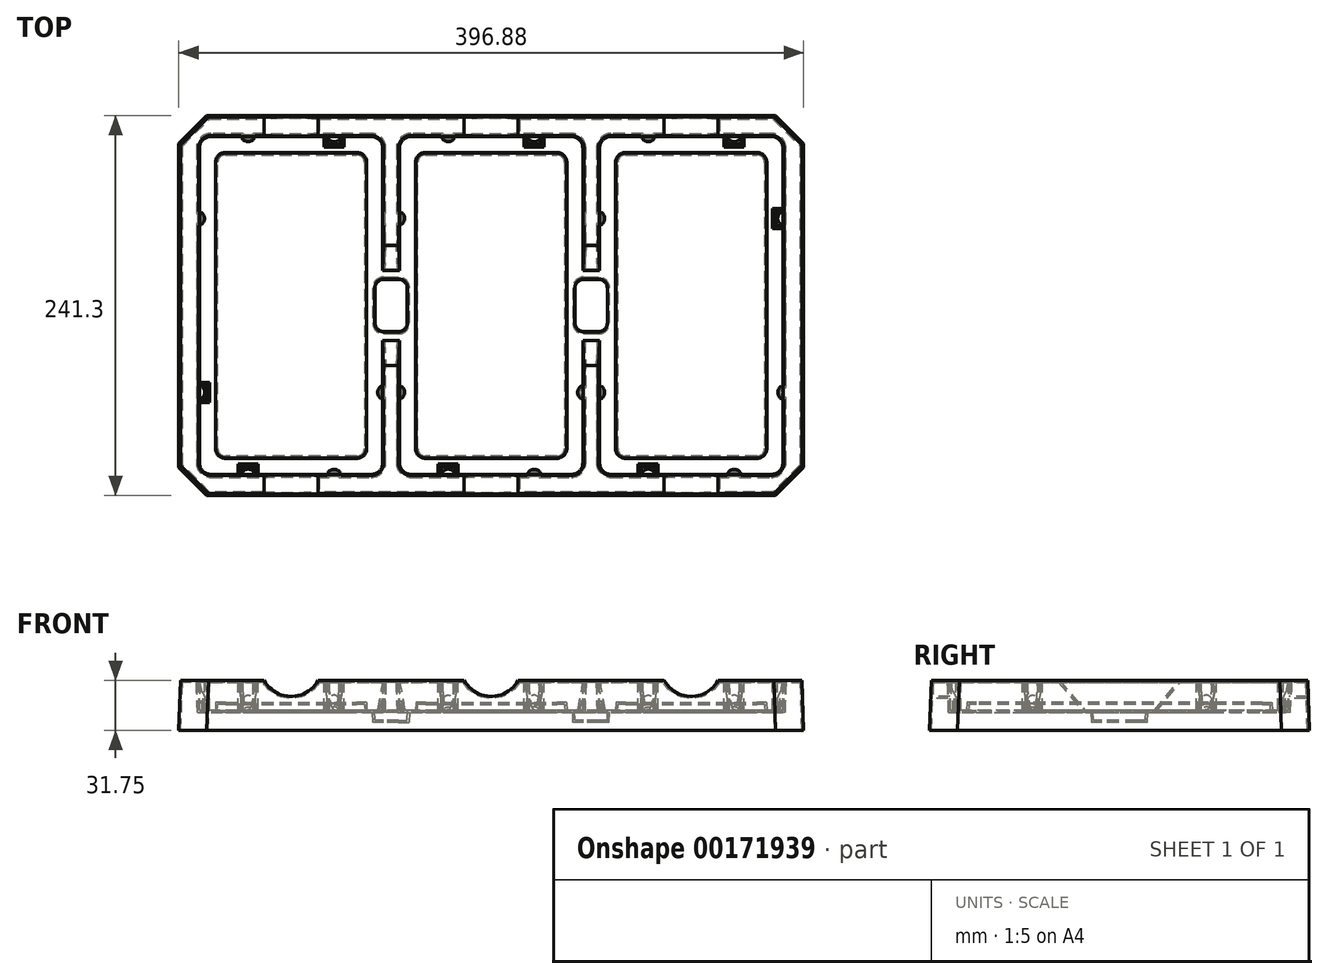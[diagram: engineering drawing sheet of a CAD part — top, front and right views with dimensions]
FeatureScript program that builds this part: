
annotation { "Feature Type Name" : "Feature", "Feature Type Description" : "" }
export const myFeature = defineFeature(function(context is Context, id is Id, definition is map)
    precondition{}
    {
        {
            var Q0;
            Q0=qCreatedBy(makeId("Top.planeOp"),FACE);
            cPlane(context, id + "F0", {"entities" : qUnion([Q0]), "cplaneType" : CPlaneType.OFFSET, "offset" : 31.75 * mm, "oppositeDirection" : true, "width" : 152.4 * mm, "height" : 152.4 * mm});
        }
        {
            var Q0;
            Q0=qCreatedBy(makeId("Top.planeOp"),FACE);
            cPlane(context, id + "F1", {"entities" : qUnion([Q0]), "cplaneType" : CPlaneType.OFFSET, "offset" : 19.05 * mm, "oppositeDirection" : true, "width" : 152.4 * mm, "height" : 152.4 * mm});
        }
        {
            var Q0;
            Q0=qCreatedBy(makeId("Right.planeOp"),FACE);
            cPlane(context, id + "F2", {"entities" : qUnion([Q0]), "cplaneType" : CPlaneType.OFFSET, "offset" : 76.2 * mm, "width" : 152.4 * mm, "height" : 152.4 * mm});
        }
        {
            var Q0;
            Q0=qCreatedBy(makeId("Top.planeOp"),FACE);
            var sketch = newSketch(context, id + "F3", { "sketchPlane" : qUnion([Q0])});
            skLineSegment(sketch, "E0.bottom", {"start": v(0, 241.3) * mm, "end": v(396.87, 241.3) * mm, "construction": true});
            skLineSegment(sketch, "E0.top", {"start": v(0, 0) * mm, "end": v(396.88, 0) * mm, "construction": true});
            skLineSegment(sketch, "E0.left", {"start": v(0, 241.3) * mm, "end": v(0, 0) * mm, "construction": true});
            skLineSegment(sketch, "E0.right", {"start": v(396.88, 241.3) * mm, "end": v(396.88, 0) * mm, "construction": true});
            skLineSegment(sketch, "E1.bottom", {"start": v(20.45, 225.43) * mm, "end": v(122.3, 225.43) * mm, "construction": true});
            skLineSegment(sketch, "E1.top", {"start": v(20.45, 15.88) * mm, "end": v(122.3, 15.88) * mm, "construction": true});
            skLineSegment(sketch, "E1.left", {"start": v(15.68, 220.66) * mm, "end": v(15.68, 20.64) * mm, "construction": true});
            skLineSegment(sketch, "E1.right", {"start": v(127.06, 220.66) * mm, "end": v(127.06, 20.64) * mm, "construction": true});
            skLineSegment(sketch, "E2.bottom", {"start": v(147.51, 225.42) * mm, "end": v(249.36, 225.42) * mm, "construction": true});
            skLineSegment(sketch, "E2.top", {"start": v(147.51, 15.88) * mm, "end": v(249.36, 15.88) * mm, "construction": true});
            skLineSegment(sketch, "E2.left", {"start": v(142.75, 220.66) * mm, "end": v(142.75, 20.64) * mm, "construction": true});
            skLineSegment(sketch, "E2.right", {"start": v(254.13, 220.66) * mm, "end": v(254.13, 20.64) * mm, "construction": true});
            skLineSegment(sketch, "E3.bottom", {"start": v(274.57, 225.43) * mm, "end": v(376.43, 225.43) * mm, "construction": true});
            skLineSegment(sketch, "E3.top", {"start": v(274.57, 15.88) * mm, "end": v(376.43, 15.88) * mm, "construction": true});
            skLineSegment(sketch, "E3.left", {"start": v(269.81, 220.66) * mm, "end": v(269.81, 20.64) * mm, "construction": true});
            skLineSegment(sketch, "E3.right", {"start": v(381.2, 220.66) * mm, "end": v(381.2, 20.64) * mm, "construction": true});
            skLineSegment(sketch, "E4", {"start": v(0, 120.65) * mm, "end": v(15.68, 120.65) * mm, "construction": true});
            skLineSegment(sketch, "E5", {"start": v(127.06, 120.65) * mm, "end": v(142.75, 120.65) * mm, "construction": true});
            skLineSegment(sketch, "E6", {"start": v(254.13, 120.65) * mm, "end": v(269.81, 120.65) * mm, "construction": true});
            skLineSegment(sketch, "E7", {"start": v(381.2, 120.65) * mm, "end": v(396.88, 120.65) * mm, "construction": true});
            skPoint(sketch, "E8.visualSharp", {"position": v(15.68, 225.43) * mm});
            skArc(sketch, "E8.filletArc", {"start": v(20.45, 225.43) * mm, "mid": v(17.08, 224.03) * mm, "end": v(15.68, 220.66) * mm, "construction": true});
            skPoint(sketch, "E9.visualSharp", {"position": v(127.06, 225.43) * mm});
            skArc(sketch, "E9.filletArc", {"start": v(127.06, 220.66) * mm, "mid": v(125.67, 224.03) * mm, "end": v(122.3, 225.43) * mm, "construction": true});
            skPoint(sketch, "E10.visualSharp", {"position": v(142.75, 225.42) * mm});
            skArc(sketch, "E10.filletArc", {"start": v(147.51, 225.42) * mm, "mid": v(144.14, 224.03) * mm, "end": v(142.75, 220.66) * mm, "construction": true});
            skPoint(sketch, "E11.visualSharp", {"position": v(254.13, 225.42) * mm});
            skArc(sketch, "E11.filletArc", {"start": v(254.13, 220.66) * mm, "mid": v(252.73, 224.03) * mm, "end": v(249.36, 225.42) * mm, "construction": true});
            skPoint(sketch, "E12.visualSharp", {"position": v(269.81, 225.43) * mm});
            skArc(sketch, "E12.filletArc", {"start": v(274.57, 225.43) * mm, "mid": v(271.2, 224.03) * mm, "end": v(269.81, 220.66) * mm, "construction": true});
            skPoint(sketch, "E13.visualSharp", {"position": v(381.2, 225.43) * mm});
            skArc(sketch, "E13.filletArc", {"start": v(381.2, 220.66) * mm, "mid": v(379.8, 224.03) * mm, "end": v(376.43, 225.43) * mm, "construction": true});
            skPoint(sketch, "E14.visualSharp", {"position": v(381.2, 15.88) * mm});
            skArc(sketch, "E14.filletArc", {"start": v(376.43, 15.87) * mm, "mid": v(379.8, 17.27) * mm, "end": v(381.2, 20.64) * mm, "construction": true});
            skPoint(sketch, "E15.visualSharp", {"position": v(269.81, 15.88) * mm});
            skArc(sketch, "E15.filletArc", {"start": v(269.81, 20.64) * mm, "mid": v(271.2, 17.27) * mm, "end": v(274.57, 15.88) * mm, "construction": true});
            skPoint(sketch, "E16.visualSharp", {"position": v(254.13, 15.88) * mm});
            skArc(sketch, "E16.filletArc", {"start": v(249.36, 15.88) * mm, "mid": v(252.73, 17.27) * mm, "end": v(254.13, 20.64) * mm, "construction": true});
            skPoint(sketch, "E17.visualSharp", {"position": v(142.75, 15.88) * mm});
            skArc(sketch, "E17.filletArc", {"start": v(142.75, 20.64) * mm, "mid": v(144.14, 17.27) * mm, "end": v(147.51, 15.88) * mm, "construction": true});
            skPoint(sketch, "E18.visualSharp", {"position": v(127.06, 15.88) * mm});
            skArc(sketch, "E18.filletArc", {"start": v(122.3, 15.87) * mm, "mid": v(125.67, 17.27) * mm, "end": v(127.06, 20.64) * mm, "construction": true});
            skPoint(sketch, "E19.visualSharp", {"position": v(15.68, 15.88) * mm});
            skArc(sketch, "E19.filletArc", {"start": v(15.68, 20.64) * mm, "mid": v(17.08, 17.27) * mm, "end": v(20.45, 15.88) * mm, "construction": true});
            skSolve(sketch);
        }
        {
            var Q0;
            Q0=qCreatedBy(id+"F0.planeOp",FACE);
            var sketch = newSketch(context, id + "F4", { "sketchPlane" : qUnion([Q0])});
            skLineSegment(sketch, "E20.0", {"start": v(0, 241.3) * mm, "end": v(0, 0) * mm});
            skLineSegment(sketch, "E20.1", {"start": v(0, 241.3) * mm, "end": v(396.87, 241.3) * mm});
            skLineSegment(sketch, "E20.2", {"start": v(396.88, 241.3) * mm, "end": v(396.88, 0) * mm});
            skLineSegment(sketch, "E20.3", {"start": v(0, 0) * mm, "end": v(396.88, 0) * mm});
            skSolve(sketch);
        }
        {
            var Q0;
            Q0=qCreatedBy(id+"F1.planeOp",FACE);
            var sketch = newSketch(context, id + "F5", { "sketchPlane" : qUnion([Q0])});
            skLineSegment(sketch, "E21.0", {"start": v(147.51, 225.42) * mm, "end": v(249.36, 225.42) * mm, "construction": true});
            skArc(sketch, "E21.1", {"start": v(147.51, 225.42) * mm, "mid": v(144.14, 224.03) * mm, "end": v(142.75, 220.66) * mm, "construction": true});
            skLineSegment(sketch, "E21.2", {"start": v(142.75, 220.66) * mm, "end": v(142.75, 20.64) * mm, "construction": true});
            skLineSegment(sketch, "E21.3", {"start": v(127.06, 220.66) * mm, "end": v(127.06, 20.64) * mm, "construction": true});
            skArc(sketch, "E21.4", {"start": v(127.06, 220.66) * mm, "mid": v(125.67, 224.03) * mm, "end": v(122.3, 225.43) * mm, "construction": true});
            skLineSegment(sketch, "E21.5", {"start": v(20.45, 225.43) * mm, "end": v(122.3, 225.43) * mm, "construction": true});
            skArc(sketch, "E21.6", {"start": v(20.45, 225.43) * mm, "mid": v(17.08, 224.03) * mm, "end": v(15.68, 220.66) * mm, "construction": true});
            skLineSegment(sketch, "E21.7", {"start": v(15.68, 220.66) * mm, "end": v(15.68, 20.64) * mm, "construction": true});
            skArc(sketch, "E21.8", {"start": v(254.13, 220.66) * mm, "mid": v(252.73, 224.03) * mm, "end": v(249.36, 225.42) * mm, "construction": true});
            skArc(sketch, "E21.9", {"start": v(274.57, 225.43) * mm, "mid": v(271.2, 224.03) * mm, "end": v(269.81, 220.66) * mm, "construction": true});
            skLineSegment(sketch, "E21.10", {"start": v(269.81, 220.66) * mm, "end": v(269.81, 20.64) * mm, "construction": true});
            skLineSegment(sketch, "E21.11", {"start": v(254.13, 220.66) * mm, "end": v(254.13, 20.64) * mm, "construction": true});
            skLineSegment(sketch, "E21.12", {"start": v(274.57, 225.43) * mm, "end": v(376.43, 225.43) * mm, "construction": true});
            skArc(sketch, "E21.13", {"start": v(381.2, 220.66) * mm, "mid": v(379.8, 224.03) * mm, "end": v(376.43, 225.43) * mm, "construction": true});
            skLineSegment(sketch, "E21.14", {"start": v(381.2, 220.66) * mm, "end": v(381.2, 20.64) * mm, "construction": true});
            skArc(sketch, "E21.15", {"start": v(376.43, 15.87) * mm, "mid": v(379.8, 17.27) * mm, "end": v(381.2, 20.64) * mm, "construction": true});
            skLineSegment(sketch, "E21.16", {"start": v(274.57, 15.88) * mm, "end": v(376.43, 15.88) * mm, "construction": true});
            skArc(sketch, "E21.17", {"start": v(249.36, 15.88) * mm, "mid": v(252.73, 17.27) * mm, "end": v(254.13, 20.64) * mm, "construction": true});
            skArc(sketch, "E21.18", {"start": v(269.81, 20.64) * mm, "mid": v(271.2, 17.27) * mm, "end": v(274.57, 15.88) * mm, "construction": true});
            skLineSegment(sketch, "E21.19", {"start": v(147.51, 15.88) * mm, "end": v(249.36, 15.88) * mm, "construction": true});
            skArc(sketch, "E21.20", {"start": v(142.75, 20.64) * mm, "mid": v(144.14, 17.27) * mm, "end": v(147.51, 15.88) * mm, "construction": true});
            skArc(sketch, "E21.21", {"start": v(122.3, 15.87) * mm, "mid": v(125.67, 17.27) * mm, "end": v(127.06, 20.64) * mm, "construction": true});
            skLineSegment(sketch, "E21.22", {"start": v(20.45, 15.88) * mm, "end": v(122.3, 15.88) * mm, "construction": true});
            skArc(sketch, "E21.23", {"start": v(15.68, 20.64) * mm, "mid": v(17.08, 17.27) * mm, "end": v(20.45, 15.88) * mm, "construction": true});
            skArc(sketch, "E22.0", {"start": v(13.14, 20.64) * mm, "mid": v(15.28, 15.47) * mm, "end": v(20.45, 13.33) * mm});
            skLineSegment(sketch, "E22.1", {"start": v(13.14, 220.66) * mm, "end": v(13.14, 20.64) * mm});
            skLineSegment(sketch, "E22.2", {"start": v(20.45, 13.33) * mm, "end": v(122.3, 13.33) * mm});
            skArc(sketch, "E22.3", {"start": v(20.45, 227.97) * mm, "mid": v(15.28, 225.83) * mm, "end": v(13.14, 220.66) * mm});
            skArc(sketch, "E22.4", {"start": v(122.3, 13.33) * mm, "mid": v(127.46, 15.47) * mm, "end": v(129.6, 20.64) * mm});
            skLineSegment(sketch, "E22.5", {"start": v(129.6, 220.66) * mm, "end": v(129.6, 20.64) * mm});
            skArc(sketch, "E22.6", {"start": v(129.6, 220.66) * mm, "mid": v(127.46, 225.83) * mm, "end": v(122.3, 227.97) * mm});
            skLineSegment(sketch, "E22.7", {"start": v(20.45, 227.97) * mm, "end": v(122.3, 227.97) * mm});
            skArc(sketch, "E23.0", {"start": v(140.2, 20.64) * mm, "mid": v(142.35, 15.47) * mm, "end": v(147.51, 13.34) * mm});
            skLineSegment(sketch, "E23.1", {"start": v(140.2, 220.66) * mm, "end": v(140.2, 20.64) * mm});
            skLineSegment(sketch, "E23.2", {"start": v(147.51, 13.34) * mm, "end": v(249.36, 13.34) * mm});
            skArc(sketch, "E23.3", {"start": v(147.51, 227.96) * mm, "mid": v(142.35, 225.83) * mm, "end": v(140.2, 220.66) * mm});
            skArc(sketch, "E23.4", {"start": v(249.36, 13.34) * mm, "mid": v(254.53, 15.47) * mm, "end": v(256.67, 20.64) * mm});
            skLineSegment(sketch, "E23.5", {"start": v(256.67, 220.66) * mm, "end": v(256.67, 20.64) * mm});
            skArc(sketch, "E23.6", {"start": v(256.67, 220.66) * mm, "mid": v(254.53, 225.83) * mm, "end": v(249.36, 227.96) * mm});
            skLineSegment(sketch, "E23.7", {"start": v(147.51, 227.96) * mm, "end": v(249.36, 227.96) * mm});
            skArc(sketch, "E24.0", {"start": v(383.73, 220.66) * mm, "mid": v(381.6, 225.83) * mm, "end": v(376.43, 227.97) * mm});
            skLineSegment(sketch, "E24.1", {"start": v(274.57, 227.97) * mm, "end": v(376.43, 227.97) * mm});
            skLineSegment(sketch, "E24.2", {"start": v(383.73, 220.66) * mm, "end": v(383.73, 20.64) * mm});
            skArc(sketch, "E24.3", {"start": v(274.57, 227.97) * mm, "mid": v(269.41, 225.83) * mm, "end": v(267.27, 220.66) * mm});
            skArc(sketch, "E24.4", {"start": v(376.43, 13.34) * mm, "mid": v(381.6, 15.47) * mm, "end": v(383.73, 20.64) * mm});
            skLineSegment(sketch, "E24.5", {"start": v(274.57, 13.34) * mm, "end": v(376.43, 13.34) * mm});
            skArc(sketch, "E24.6", {"start": v(267.27, 20.64) * mm, "mid": v(269.41, 15.47) * mm, "end": v(274.57, 13.34) * mm});
            skLineSegment(sketch, "E24.7", {"start": v(267.27, 220.66) * mm, "end": v(267.27, 20.64) * mm});
            skSolve(sketch);
        }
        {
            var Q0;
            Q0=qCreatedBy(id+"F1.planeOp",FACE);
            var sketch = newSketch(context, id + "F6", { "sketchPlane" : qUnion([Q0])});
            skLineSegment(sketch, "E25", {"start": v(15.68, 225.43) * mm, "end": v(127.06, 15.87) * mm, "construction": true});
            skLineSegment(sketch, "E26", {"start": v(142.75, 225.43) * mm, "end": v(254.13, 15.88) * mm, "construction": true});
            skLineSegment(sketch, "E27", {"start": v(269.81, 225.43) * mm, "end": v(381.2, 15.87) * mm, "construction": true});
            skLineSegment(sketch, "E28.bottom", {"start": v(29.65, 23.5) * mm, "end": v(113.1, 23.5) * mm});
            skLineSegment(sketch, "E28.top", {"start": v(29.65, 217.8) * mm, "end": v(113.1, 217.8) * mm});
            skLineSegment(sketch, "E28.left", {"start": v(23.3, 29.85) * mm, "end": v(23.3, 211.45) * mm});
            skLineSegment(sketch, "E28.right", {"start": v(119.44, 29.85) * mm, "end": v(119.44, 211.45) * mm});
            skPoint(sketch, "E28.middle", {"position": v(71.37, 120.65) * mm});
            skLineSegment(sketch, "E29.bottom", {"start": v(156.72, 23.5) * mm, "end": v(240.16, 23.5) * mm});
            skLineSegment(sketch, "E29.top", {"start": v(156.72, 217.8) * mm, "end": v(240.16, 217.8) * mm});
            skLineSegment(sketch, "E29.left", {"start": v(150.37, 29.85) * mm, "end": v(150.37, 211.45) * mm});
            skLineSegment(sketch, "E29.right", {"start": v(246.5, 29.85) * mm, "end": v(246.5, 211.45) * mm});
            skPoint(sketch, "E29.middle", {"position": v(198.44, 120.65) * mm});
            skLineSegment(sketch, "E30.bottom", {"start": v(283.78, 23.5) * mm, "end": v(367.22, 23.5) * mm});
            skLineSegment(sketch, "E30.top", {"start": v(283.78, 217.8) * mm, "end": v(367.22, 217.8) * mm});
            skLineSegment(sketch, "E30.left", {"start": v(277.43, 29.85) * mm, "end": v(277.43, 211.45) * mm});
            skLineSegment(sketch, "E30.right", {"start": v(373.57, 29.85) * mm, "end": v(373.57, 211.45) * mm});
            skPoint(sketch, "E30.middle", {"position": v(325.5, 120.65) * mm});
            skPoint(sketch, "E31.visualSharp", {"position": v(23.3, 217.8) * mm});
            skArc(sketch, "E31.filletArc", {"start": v(29.65, 217.8) * mm, "mid": v(25.16, 215.95) * mm, "end": v(23.3, 211.45) * mm});
            skPoint(sketch, "E32.visualSharp", {"position": v(119.44, 217.8) * mm});
            skArc(sketch, "E32.filletArc", {"start": v(119.44, 211.45) * mm, "mid": v(117.58, 215.95) * mm, "end": v(113.1, 217.8) * mm});
            skPoint(sketch, "E33.visualSharp", {"position": v(150.37, 217.8) * mm});
            skArc(sketch, "E33.filletArc", {"start": v(156.72, 217.8) * mm, "mid": v(152.23, 215.95) * mm, "end": v(150.37, 211.45) * mm});
            skPoint(sketch, "E34.visualSharp", {"position": v(246.5, 217.8) * mm});
            skArc(sketch, "E34.filletArc", {"start": v(246.5, 211.45) * mm, "mid": v(244.65, 215.95) * mm, "end": v(240.16, 217.8) * mm});
            skPoint(sketch, "E35.visualSharp", {"position": v(277.43, 217.8) * mm});
            skArc(sketch, "E35.filletArc", {"start": v(283.78, 217.8) * mm, "mid": v(279.3, 215.95) * mm, "end": v(277.43, 211.45) * mm});
            skPoint(sketch, "E36.visualSharp", {"position": v(373.57, 217.8) * mm});
            skArc(sketch, "E36.filletArc", {"start": v(373.57, 211.45) * mm, "mid": v(371.71, 215.95) * mm, "end": v(367.22, 217.8) * mm});
            skPoint(sketch, "E37.visualSharp", {"position": v(373.57, 23.5) * mm});
            skArc(sketch, "E37.filletArc", {"start": v(367.22, 23.5) * mm, "mid": v(371.71, 25.35) * mm, "end": v(373.57, 29.85) * mm});
            skPoint(sketch, "E38.visualSharp", {"position": v(277.43, 23.5) * mm});
            skArc(sketch, "E38.filletArc", {"start": v(277.43, 29.85) * mm, "mid": v(279.3, 25.35) * mm, "end": v(283.78, 23.5) * mm});
            skPoint(sketch, "E39.visualSharp", {"position": v(246.5, 23.5) * mm});
            skArc(sketch, "E39.filletArc", {"start": v(240.16, 23.5) * mm, "mid": v(244.65, 25.35) * mm, "end": v(246.5, 29.85) * mm});
            skPoint(sketch, "E40.visualSharp", {"position": v(150.37, 23.5) * mm});
            skArc(sketch, "E40.filletArc", {"start": v(150.37, 29.85) * mm, "mid": v(152.23, 25.35) * mm, "end": v(156.72, 23.5) * mm});
            skPoint(sketch, "E41.visualSharp", {"position": v(119.44, 23.5) * mm});
            skArc(sketch, "E41.filletArc", {"start": v(113.1, 23.5) * mm, "mid": v(117.58, 25.35) * mm, "end": v(119.44, 29.85) * mm});
            skPoint(sketch, "E42.visualSharp", {"position": v(23.3, 23.5) * mm});
            skArc(sketch, "E42.filletArc", {"start": v(23.3, 29.85) * mm, "mid": v(25.16, 25.35) * mm, "end": v(29.65, 23.5) * mm});
            skSolve(sketch);
        }
        {
            var Q0;
            Q0=makeQuery(id+"F4.imprint","IMPRINT",FACE,{"disambiguationData":[TD([[makeQuery(id+"F4.imprint","IMPRINT",EDGE,{"derivedFrom":sQuery(id+"F4.wireOp",EDGE,"E20.0")}),1.0]])]});
            extrude(context, id + "F7", {"entities" : qUnion([Q0]), "depth" : 31.75 * mm, "hasDraft" : true, "draftAngle" : 2 * degree, "draftPullDirection" : true});
        }
        {
            var Q0;
            Q0=qCreatedBy(makeId("Top.planeOp"),FACE);
            var sketch = newSketch(context, id + "F8", { "sketchPlane" : qUnion([Q0])});
            skLineSegment(sketch, "E43.0.0", {"start": v(13.14, 220.66) * mm, "end": v(13.14, 20.64) * mm, "construction": true});
            skArc(sketch, "E43.0.1", {"start": v(13.14, 20.64) * mm, "mid": v(15.28, 15.47) * mm, "end": v(20.45, 13.33) * mm, "construction": true});
            skLineSegment(sketch, "E43.0.2", {"start": v(20.45, 13.33) * mm, "end": v(122.3, 13.33) * mm, "construction": true});
            skArc(sketch, "E43.0.3", {"start": v(122.3, 13.33) * mm, "mid": v(127.46, 15.47) * mm, "end": v(129.6, 20.64) * mm, "construction": true});
            skLineSegment(sketch, "E43.0.4", {"start": v(129.6, 20.64) * mm, "end": v(129.6, 220.66) * mm, "construction": true});
            skArc(sketch, "E43.0.5", {"start": v(129.6, 220.66) * mm, "mid": v(127.46, 225.83) * mm, "end": v(122.3, 227.97) * mm, "construction": true});
            skLineSegment(sketch, "E43.0.6", {"start": v(122.3, 227.97) * mm, "end": v(20.45, 227.97) * mm, "construction": true});
            skArc(sketch, "E43.0.7", {"start": v(20.45, 227.97) * mm, "mid": v(15.28, 225.83) * mm, "end": v(13.14, 220.66) * mm, "construction": true});
            skLineSegment(sketch, "E44.0.0", {"start": v(140.2, 220.66) * mm, "end": v(140.2, 20.64) * mm, "construction": true});
            skArc(sketch, "E44.0.1", {"start": v(140.2, 20.64) * mm, "mid": v(142.35, 15.47) * mm, "end": v(147.51, 13.34) * mm, "construction": true});
            skLineSegment(sketch, "E44.0.2", {"start": v(147.51, 13.34) * mm, "end": v(249.36, 13.34) * mm, "construction": true});
            skArc(sketch, "E44.0.3", {"start": v(249.36, 13.34) * mm, "mid": v(254.53, 15.47) * mm, "end": v(256.67, 20.64) * mm, "construction": true});
            skLineSegment(sketch, "E44.0.4", {"start": v(256.67, 20.64) * mm, "end": v(256.67, 220.66) * mm, "construction": true});
            skArc(sketch, "E44.0.5", {"start": v(256.67, 220.66) * mm, "mid": v(254.53, 225.83) * mm, "end": v(249.36, 227.96) * mm, "construction": true});
            skLineSegment(sketch, "E44.0.6", {"start": v(249.36, 227.96) * mm, "end": v(147.51, 227.96) * mm, "construction": true});
            skArc(sketch, "E44.0.7", {"start": v(147.51, 227.96) * mm, "mid": v(142.35, 225.83) * mm, "end": v(140.2, 220.66) * mm, "construction": true});
            skLineSegment(sketch, "E44.1.0", {"start": v(383.73, 20.64) * mm, "end": v(383.73, 220.66) * mm, "construction": true});
            skArc(sketch, "E44.1.1", {"start": v(383.73, 220.66) * mm, "mid": v(381.6, 225.83) * mm, "end": v(376.43, 227.97) * mm, "construction": true});
            skLineSegment(sketch, "E44.1.2", {"start": v(376.43, 227.97) * mm, "end": v(274.57, 227.97) * mm, "construction": true});
            skArc(sketch, "E44.1.3", {"start": v(274.57, 227.97) * mm, "mid": v(269.41, 225.83) * mm, "end": v(267.27, 220.66) * mm, "construction": true});
            skLineSegment(sketch, "E44.1.4", {"start": v(267.27, 220.66) * mm, "end": v(267.27, 20.64) * mm, "construction": true});
            skArc(sketch, "E44.1.5", {"start": v(267.27, 20.64) * mm, "mid": v(269.41, 15.47) * mm, "end": v(274.57, 13.34) * mm, "construction": true});
            skLineSegment(sketch, "E44.1.6", {"start": v(274.57, 13.34) * mm, "end": v(376.43, 13.34) * mm, "construction": true});
            skArc(sketch, "E44.1.7", {"start": v(376.43, 13.34) * mm, "mid": v(381.6, 15.47) * mm, "end": v(383.73, 20.64) * mm, "construction": true});
            skLineSegment(sketch, "E45.0.0", {"start": v(396.88, 241.3) * mm, "end": v(0, 241.3) * mm, "construction": true});
            skLineSegment(sketch, "E45.0.1", {"start": v(0, 241.3) * mm, "end": v(0, 0) * mm, "construction": true});
            skLineSegment(sketch, "E45.0.2", {"start": v(0, 0) * mm, "end": v(396.88, 0) * mm, "construction": true});
            skLineSegment(sketch, "E45.0.3", {"start": v(396.88, 0) * mm, "end": v(396.88, 241.3) * mm, "construction": true});
            skLineSegment(sketch, "E46", {"start": v(54.23, 227.97) * mm, "end": v(88.52, 227.97) * mm, "construction": true});
            skArc(sketch, "E47.0.startCap", {"start": v(54.23, 222.89) * mm, "mid": v(49.15, 227.97) * mm, "end": v(54.23, 233.05) * mm});
            skArc(sketch, "E47.0.endCap", {"start": v(88.52, 233.05) * mm, "mid": v(93.6, 227.97) * mm, "end": v(88.52, 222.89) * mm});
            skLineSegment(sketch, "E47.0.left", {"start": v(54.23, 233.05) * mm, "end": v(88.52, 233.05) * mm});
            skLineSegment(sketch, "E47.0.right", {"start": v(54.23, 222.89) * mm, "end": v(88.52, 222.89) * mm});
            skPoint(sketch, "E48", {"position": v(71.37, 227.97) * mm});
            skLineSegment(sketch, "E49", {"start": v(54.23, 13.33) * mm, "end": v(88.52, 13.33) * mm, "construction": true});
            skArc(sketch, "E50.0.startCap", {"start": v(54.23, 8.25) * mm, "mid": v(49.15, 13.33) * mm, "end": v(54.23, 18.41) * mm});
            skArc(sketch, "E50.0.endCap", {"start": v(88.52, 18.42) * mm, "mid": v(93.6, 13.33) * mm, "end": v(88.52, 8.25) * mm});
            skLineSegment(sketch, "E50.0.left", {"start": v(54.23, 18.41) * mm, "end": v(88.52, 18.41) * mm});
            skLineSegment(sketch, "E50.0.right", {"start": v(54.23, 8.25) * mm, "end": v(88.52, 8.25) * mm});
            skPoint(sketch, "E51", {"position": v(71.37, 13.33) * mm});
            skLineSegment(sketch, "E52", {"start": v(181.3, 227.97) * mm, "end": v(215.58, 227.97) * mm, "construction": true});
            skArc(sketch, "E53.0.startCap", {"start": v(181.3, 222.89) * mm, "mid": v(176.21, 227.97) * mm, "end": v(181.3, 233.05) * mm});
            skArc(sketch, "E53.0.endCap", {"start": v(215.58, 233.05) * mm, "mid": v(220.66, 227.97) * mm, "end": v(215.58, 222.89) * mm});
            skLineSegment(sketch, "E53.0.left", {"start": v(181.3, 233.05) * mm, "end": v(215.58, 233.05) * mm});
            skLineSegment(sketch, "E53.0.right", {"start": v(181.3, 222.89) * mm, "end": v(215.58, 222.89) * mm});
            skPoint(sketch, "E54", {"position": v(198.44, 227.97) * mm});
            skLineSegment(sketch, "E55", {"start": v(308.36, 227.97) * mm, "end": v(342.65, 227.97) * mm, "construction": true});
            skArc(sketch, "E56.0.startCap", {"start": v(308.36, 222.88) * mm, "mid": v(303.28, 227.96) * mm, "end": v(308.36, 233.04) * mm});
            skArc(sketch, "E56.0.endCap", {"start": v(342.65, 233.04) * mm, "mid": v(347.73, 227.96) * mm, "end": v(342.65, 222.88) * mm});
            skLineSegment(sketch, "E56.0.left", {"start": v(308.36, 233.04) * mm, "end": v(342.65, 233.04) * mm});
            skLineSegment(sketch, "E56.0.right", {"start": v(308.36, 222.88) * mm, "end": v(342.65, 222.88) * mm});
            skPoint(sketch, "E57", {"position": v(325.5, 227.97) * mm});
            skLineSegment(sketch, "E58", {"start": v(308.36, 13.34) * mm, "end": v(342.65, 13.34) * mm, "construction": true});
            skArc(sketch, "E59.0.startCap", {"start": v(308.36, 8.26) * mm, "mid": v(303.28, 13.34) * mm, "end": v(308.36, 18.42) * mm});
            skArc(sketch, "E59.0.endCap", {"start": v(342.65, 18.42) * mm, "mid": v(347.73, 13.34) * mm, "end": v(342.65, 8.25) * mm});
            skLineSegment(sketch, "E59.0.left", {"start": v(308.36, 18.42) * mm, "end": v(342.65, 18.42) * mm});
            skLineSegment(sketch, "E59.0.right", {"start": v(308.36, 8.26) * mm, "end": v(342.65, 8.26) * mm});
            skPoint(sketch, "E60", {"position": v(325.5, 13.34) * mm});
            skLineSegment(sketch, "E61", {"start": v(181.3, 13.34) * mm, "end": v(215.58, 13.34) * mm, "construction": true});
            skArc(sketch, "E62.0.startCap", {"start": v(181.3, 8.25) * mm, "mid": v(176.21, 13.33) * mm, "end": v(181.3, 18.41) * mm});
            skArc(sketch, "E62.0.endCap", {"start": v(215.58, 18.42) * mm, "mid": v(220.66, 13.33) * mm, "end": v(215.58, 8.25) * mm});
            skLineSegment(sketch, "E62.0.left", {"start": v(181.3, 18.41) * mm, "end": v(215.58, 18.41) * mm});
            skLineSegment(sketch, "E62.0.right", {"start": v(181.3, 8.25) * mm, "end": v(215.58, 8.25) * mm});
            skPoint(sketch, "E63", {"position": v(198.44, 13.33) * mm});
            skPoint(sketch, "E64", {"position": v(198.44, 227.96) * mm});
            skLineSegment(sketch, "E65", {"start": v(383.73, 103.5) * mm, "end": v(383.73, 137.8) * mm, "construction": true});
            skArc(sketch, "E66.0.startCap", {"start": v(388.81, 103.5) * mm, "mid": v(383.73, 98.42) * mm, "end": v(378.65, 103.5) * mm});
            skArc(sketch, "E66.0.endCap", {"start": v(378.65, 137.8) * mm, "mid": v(383.73, 142.88) * mm, "end": v(388.81, 137.8) * mm});
            skLineSegment(sketch, "E66.0.left", {"start": v(378.65, 103.5) * mm, "end": v(378.65, 137.8) * mm});
            skLineSegment(sketch, "E66.0.right", {"start": v(388.81, 103.5) * mm, "end": v(388.81, 137.8) * mm});
            skPoint(sketch, "E67", {"position": v(383.73, 120.65) * mm});
            skLineSegment(sketch, "E68", {"start": v(13.14, 103.5) * mm, "end": v(13.14, 137.8) * mm, "construction": true});
            skArc(sketch, "E69.0.startCap", {"start": v(18.22, 103.5) * mm, "mid": v(13.14, 98.43) * mm, "end": v(8.06, 103.5) * mm});
            skArc(sketch, "E69.0.endCap", {"start": v(8.06, 137.8) * mm, "mid": v(13.14, 142.88) * mm, "end": v(18.22, 137.8) * mm});
            skLineSegment(sketch, "E69.0.left", {"start": v(8.06, 103.5) * mm, "end": v(8.06, 137.8) * mm});
            skLineSegment(sketch, "E69.0.right", {"start": v(18.22, 103.5) * mm, "end": v(18.22, 137.8) * mm});
            skPoint(sketch, "E70", {"position": v(13.14, 120.65) * mm});
            skLineSegment(sketch, "E71", {"start": v(129.6, 120.65) * mm, "end": v(140.2, 120.65) * mm, "construction": true});
            skLineSegment(sketch, "E72", {"start": v(256.67, 120.65) * mm, "end": v(267.27, 120.65) * mm, "construction": true});
            skLineSegment(sketch, "E73.bottom", {"start": v(130.14, 103.19) * mm, "end": v(139.67, 103.19) * mm});
            skLineSegment(sketch, "E73.top", {"start": v(130.14, 138.11) * mm, "end": v(139.67, 138.11) * mm});
            skLineSegment(sketch, "E73.left", {"start": v(123.8, 109.54) * mm, "end": v(123.8, 131.76) * mm});
            skLineSegment(sketch, "E73.right", {"start": v(146.02, 109.54) * mm, "end": v(146.02, 131.76) * mm});
            skPoint(sketch, "E73.middle", {"position": v(134.9, 120.65) * mm});
            skLineSegment(sketch, "E74.bottom", {"start": v(257.2, 103.19) * mm, "end": v(266.73, 103.19) * mm});
            skLineSegment(sketch, "E74.top", {"start": v(257.2, 138.11) * mm, "end": v(266.73, 138.11) * mm});
            skLineSegment(sketch, "E74.left", {"start": v(250.86, 109.54) * mm, "end": v(250.86, 131.76) * mm});
            skLineSegment(sketch, "E74.right", {"start": v(273.08, 109.54) * mm, "end": v(273.08, 131.76) * mm});
            skPoint(sketch, "E74.middle", {"position": v(261.97, 120.65) * mm});
            skPoint(sketch, "E75.visualSharp", {"position": v(123.8, 138.11) * mm});
            skArc(sketch, "E75.filletArc", {"start": v(130.14, 138.11) * mm, "mid": v(125.65, 136.25) * mm, "end": v(123.8, 131.76) * mm});
            skPoint(sketch, "E76.visualSharp", {"position": v(146.02, 138.11) * mm});
            skArc(sketch, "E76.filletArc", {"start": v(146.02, 131.76) * mm, "mid": v(144.16, 136.25) * mm, "end": v(139.67, 138.11) * mm});
            skPoint(sketch, "E77.visualSharp", {"position": v(123.8, 103.19) * mm});
            skArc(sketch, "E77.filletArc", {"start": v(123.8, 109.54) * mm, "mid": v(125.65, 105.05) * mm, "end": v(130.14, 103.19) * mm});
            skPoint(sketch, "E78.visualSharp", {"position": v(146.02, 103.19) * mm});
            skArc(sketch, "E78.filletArc", {"start": v(139.67, 103.19) * mm, "mid": v(144.16, 105.05) * mm, "end": v(146.02, 109.54) * mm});
            skPoint(sketch, "E79.visualSharp", {"position": v(250.86, 138.11) * mm});
            skArc(sketch, "E79.filletArc", {"start": v(257.2, 138.11) * mm, "mid": v(252.72, 136.25) * mm, "end": v(250.86, 131.76) * mm});
            skPoint(sketch, "E80.visualSharp", {"position": v(273.08, 138.11) * mm});
            skArc(sketch, "E80.filletArc", {"start": v(273.08, 131.76) * mm, "mid": v(271.22, 136.25) * mm, "end": v(266.73, 138.11) * mm});
            skPoint(sketch, "E81.visualSharp", {"position": v(273.08, 103.19) * mm});
            skArc(sketch, "E81.filletArc", {"start": v(266.73, 103.19) * mm, "mid": v(271.22, 105.05) * mm, "end": v(273.08, 109.54) * mm});
            skPoint(sketch, "E82.visualSharp", {"position": v(250.86, 103.19) * mm});
            skArc(sketch, "E82.filletArc", {"start": v(250.86, 109.54) * mm, "mid": v(252.72, 105.05) * mm, "end": v(257.2, 103.19) * mm});
            skSolve(sketch);
        }
        {
            var Q0;
            Q0=makeQuery(id+"F5.imprint","IMPRINT",FACE,{"disambiguationData":[TD([[makeQuery(id+"F5.imprint","IMPRINT",EDGE,{"derivedFrom":sQuery(id+"F5.wireOp",EDGE,"E22.0")}),1.0]])]});
            var Q1;
            Q1=makeQuery(id+"F5.imprint","IMPRINT",FACE,{"disambiguationData":[TD([[makeQuery(id+"F5.imprint","IMPRINT",EDGE,{"derivedFrom":sQuery(id+"F5.wireOp",EDGE,"E23.0")}),1.0]])]});
            var Q2;
            Q2=makeQuery(id+"F5.imprint","IMPRINT",FACE,{"disambiguationData":[TD([[makeQuery(id+"F5.imprint","IMPRINT",EDGE,{"derivedFrom":sQuery(id+"F5.wireOp",EDGE,"E24.0")}),1.0]])]});
            extrude(context, id + "F9", {"entities" : qUnion([Q0, Q1, Q2]), "operationType" : NewBodyOperationType.REMOVE, "endBound" : BoundingType.THROUGH_ALL, "depth" : 25.4 * mm, "hasDraft" : true, "draftAngle" : 2 * degree});
        }
        {
            var Q0;
            Q0=makeQuery(id+"F8.imprint","IMPRINT",FACE,{"disambiguationData":[TD([[makeQuery(id+"F8.imprint","IMPRINT",EDGE,{"derivedFrom":sQuery(id+"F8.wireOp",EDGE,"E47.0.startCap")}),-1.0]])]});
            var Q1;
            Q1=makeQuery(id+"F8.imprint","IMPRINT",FACE,{"disambiguationData":[TD([[makeQuery(id+"F8.imprint","IMPRINT",EDGE,{"derivedFrom":sQuery(id+"F8.wireOp",EDGE,"E53.0.startCap")}),-1.0]])]});
            var Q2;
            Q2=makeQuery(id+"F8.imprint","IMPRINT",FACE,{"disambiguationData":[TD([[makeQuery(id+"F8.imprint","IMPRINT",EDGE,{"derivedFrom":sQuery(id+"F8.wireOp",EDGE,"E56.0.startCap")}),-1.0]])]});
            var Q3;
            Q3=makeQuery(id+"F8.imprint","IMPRINT",FACE,{"disambiguationData":[TD([[makeQuery(id+"F8.imprint","IMPRINT",EDGE,{"derivedFrom":sQuery(id+"F8.wireOp",EDGE,"E66.0.startCap")}),-1.0]])]});
            var Q4;
            Q4=makeQuery(id+"F8.imprint","IMPRINT",FACE,{"disambiguationData":[TD([[makeQuery(id+"F8.imprint","IMPRINT",EDGE,{"derivedFrom":sQuery(id+"F8.wireOp",EDGE,"E69.0.startCap")}),-1.0]])]});
            var Q5;
            Q5=makeQuery(id+"F8.imprint","IMPRINT",FACE,{"disambiguationData":[TD([[makeQuery(id+"F8.imprint","IMPRINT",EDGE,{"derivedFrom":sQuery(id+"F8.wireOp",EDGE,"E50.0.startCap")}),-1.0]])]});
            var Q6;
            Q6=makeQuery(id+"F8.imprint","IMPRINT",FACE,{"disambiguationData":[TD([[makeQuery(id+"F8.imprint","IMPRINT",EDGE,{"derivedFrom":sQuery(id+"F8.wireOp",EDGE,"E62.0.startCap")}),-1.0]])]});
            var Q7;
            Q7=makeQuery(id+"F8.imprint","IMPRINT",FACE,{"disambiguationData":[TD([[makeQuery(id+"F8.imprint","IMPRINT",EDGE,{"derivedFrom":sQuery(id+"F8.wireOp",EDGE,"E59.0.startCap")}),-1.0]])]});
            var Q8;
            Q8=makeQuery(id+"F8.imprint","IMPRINT",FACE,{"disambiguationData":[TD([[makeQuery(id+"F8.imprint","IMPRINT",EDGE,{"derivedFrom":sQuery(id+"F8.wireOp",EDGE,"E73.bottom")}),1.0]])]});
            var Q9;
            Q9=makeQuery(id+"F8.imprint","IMPRINT",FACE,{"disambiguationData":[TD([[makeQuery(id+"F8.imprint","IMPRINT",EDGE,{"derivedFrom":sQuery(id+"F8.wireOp",EDGE,"E74.bottom")}),1.0]])]});
            extrude(context, id + "F10", {"entities" : qUnion([Q0, Q1, Q2, Q3, Q4, Q5, Q6, Q7, Q8, Q9]), "operationType" : NewBodyOperationType.REMOVE, "oppositeDirection" : true, "depth" : 25.4 * mm, "hasDraft" : true, "draftAngle" : 2 * degree, "draftPullDirection" : true});
        }
        {
            var Q0;
            Q0=qCreatedBy(id+"F2.planeOp",FACE);
            var sketch = newSketch(context, id + "F11", { "sketchPlane" : qUnion([Q0])});
            skPoint(sketch, "E83.0", {"position": v(120.65, 0) * mm});
            skLineSegment(sketch, "E84", {"start": v(82.55, 0) * mm, "end": v(158.75, 0) * mm});
            skLineSegment(sketch, "E85", {"start": v(82.55, 0) * mm, "end": v(98.53, -19.05) * mm});
            skLineSegment(sketch, "E86", {"start": v(98.53, -19.05) * mm, "end": v(142.77, -19.05) * mm});
            skLineSegment(sketch, "E87", {"start": v(142.77, -19.05) * mm, "end": v(158.75, 0) * mm});
            skPoint(sketch, "E88", {"position": v(120.65, -19.05) * mm});
            skLineSegment(sketch, "E89", {"start": v(82.55, 0) * mm, "end": v(82.55, -19.05) * mm, "construction": true});
            skSolve(sketch);
        }
        {
            var Q0;
            Q0=qCreatedBy(makeId("Front.planeOp"),FACE);
            var sketch = newSketch(context, id + "F12", { "sketchPlane" : qUnion([Q0])});
            skLineSegment(sketch, "E90.0", {"start": v(54.23, 0) * mm, "end": v(88.52, 0) * mm, "construction": true});
            skLineSegment(sketch, "E90.1", {"start": v(181.3, 0) * mm, "end": v(215.58, 0) * mm, "construction": true});
            skLineSegment(sketch, "E91.0", {"start": v(308.36, 0) * mm, "end": v(342.65, 0) * mm, "construction": true});
            skCircle(sketch, "E92", {"center": v(71.37, 9.39) * mm, "radius": 19.55 * mm});
            skPoint(sketch, "E92.centerSnap0", {"position": v(71.37, 0) * mm});
            skCircle(sketch, "E93", {"center": v(325.5, 9.39) * mm, "radius": 19.55 * mm});
            skPoint(sketch, "E93.centerSnap0", {"position": v(325.5, 0) * mm});
            skCircle(sketch, "E94", {"center": v(198.44, 9.39) * mm, "radius": 19.55 * mm});
            skPoint(sketch, "E94.centerSnap0", {"position": v(198.44, 0) * mm});
            skLineSegment(sketch, "E95", {"start": v(71.37, 0) * mm, "end": v(71.37, -10.16) * mm});
            skSolve(sketch);
        }
        {
            var Q0;
            Q0=makeQuery(id+"F12.imprint","IMPRINT",FACE,{"disambiguationData":[TD([[makeQuery(id+"F12.imprint","IMPRINT",EDGE,{"derivedFrom":sQuery(id+"F12.wireOp",EDGE,"E92")}),1.0]])]});
            var Q1;
            Q1=makeQuery(id+"F12.imprint","IMPRINT",FACE,{"disambiguationData":[TD([[makeQuery(id+"F12.imprint","IMPRINT",EDGE,{"derivedFrom":sQuery(id+"F12.wireOp",EDGE,"E94")}),1.0]])]});
            var Q2;
            Q2=makeQuery(id+"F12.imprint","IMPRINT",FACE,{"disambiguationData":[TD([[makeQuery(id+"F12.imprint","IMPRINT",EDGE,{"derivedFrom":sQuery(id+"F12.wireOp",EDGE,"E93")}),1.0]])]});
            extrude(context, id + "F13", {"entities" : qUnion([Q0, Q1, Q2]), "operationType" : NewBodyOperationType.REMOVE, "endBound" : BoundingType.THROUGH_ALL, "oppositeDirection" : true, "depth" : 25.4 * mm});
        }
        {
            var Q0;
            Q0=makeQuery(id+"F11.imprint","IMPRINT",FACE,{"disambiguationData":[TD([[makeQuery(id+"F11.imprint","IMPRINT",EDGE,{"derivedFrom":sQuery(id+"F11.wireOp",EDGE,"E84")}),-1.0]])]});
            extrude(context, id + "F14", {"entities" : qUnion([Q0]), "operationType" : NewBodyOperationType.REMOVE, "depth" : 254 * mm});
        }
        {
            var Q0;
            Q0=qCreatedBy(makeId("Top.planeOp"),FACE);
            var sketch = newSketch(context, id + "F15", { "sketchPlane" : qUnion([Q0])});
            skArc(sketch, "E96.0", {"start": v(18.22, 103.5) * mm, "mid": v(13.14, 98.43) * mm, "end": v(8.06, 103.5) * mm, "construction": true});
            skArc(sketch, "E96.1", {"start": v(8.06, 137.8) * mm, "mid": v(13.14, 142.88) * mm, "end": v(18.22, 137.8) * mm, "construction": true});
            skArc(sketch, "E96.2", {"start": v(54.23, 8.25) * mm, "mid": v(49.15, 13.33) * mm, "end": v(54.23, 18.41) * mm, "construction": true});
            skArc(sketch, "E96.3", {"start": v(88.52, 18.42) * mm, "mid": v(93.6, 13.33) * mm, "end": v(88.52, 8.25) * mm, "construction": true});
            skLineSegment(sketch, "E96.4", {"start": v(13.14, 220.66) * mm, "end": v(13.14, 20.64) * mm, "construction": true});
            skLineSegment(sketch, "E96.5", {"start": v(20.45, 13.33) * mm, "end": v(122.3, 13.33) * mm, "construction": true});
            skLineSegment(sketch, "E96.6", {"start": v(129.6, 20.64) * mm, "end": v(129.6, 220.66) * mm, "construction": true});
            skLineSegment(sketch, "E96.7", {"start": v(122.3, 227.97) * mm, "end": v(20.45, 227.97) * mm, "construction": true});
            skArc(sketch, "E96.8", {"start": v(88.52, 233.05) * mm, "mid": v(93.6, 227.97) * mm, "end": v(88.52, 222.89) * mm, "construction": true});
            skArc(sketch, "E96.9", {"start": v(54.23, 222.89) * mm, "mid": v(49.15, 227.97) * mm, "end": v(54.23, 233.05) * mm, "construction": true});
            skLineSegment(sketch, "E96.10", {"start": v(130.14, 103.19) * mm, "end": v(139.67, 103.19) * mm, "construction": true});
            skLineSegment(sketch, "E96.11", {"start": v(130.14, 138.11) * mm, "end": v(139.67, 138.11) * mm, "construction": true});
            skLineSegment(sketch, "E97.0", {"start": v(140.2, 220.66) * mm, "end": v(140.2, 20.64) * mm, "construction": true});
            skLineSegment(sketch, "E97.1", {"start": v(147.51, 13.34) * mm, "end": v(249.36, 13.34) * mm, "construction": true});
            skLineSegment(sketch, "E97.2", {"start": v(267.27, 220.66) * mm, "end": v(267.27, 20.64) * mm, "construction": true});
            skLineSegment(sketch, "E97.3", {"start": v(256.67, 20.64) * mm, "end": v(256.67, 220.66) * mm, "construction": true});
            skLineSegment(sketch, "E97.4", {"start": v(274.57, 13.34) * mm, "end": v(376.43, 13.34) * mm, "construction": true});
            skLineSegment(sketch, "E97.5", {"start": v(249.36, 227.96) * mm, "end": v(147.51, 227.96) * mm, "construction": true});
            skLineSegment(sketch, "E97.6", {"start": v(376.43, 227.97) * mm, "end": v(274.57, 227.97) * mm, "construction": true});
            skLineSegment(sketch, "E97.7", {"start": v(383.73, 20.64) * mm, "end": v(383.73, 220.66) * mm, "construction": true});
            skArc(sketch, "E98.0", {"start": v(181.3, 222.89) * mm, "mid": v(176.21, 227.97) * mm, "end": v(181.3, 233.05) * mm, "construction": true});
            skArc(sketch, "E98.1", {"start": v(215.58, 233.05) * mm, "mid": v(220.66, 227.97) * mm, "end": v(215.58, 222.89) * mm, "construction": true});
            skLineSegment(sketch, "E98.2", {"start": v(257.2, 138.11) * mm, "end": v(266.73, 138.11) * mm, "construction": true});
            skLineSegment(sketch, "E98.3", {"start": v(257.2, 103.19) * mm, "end": v(266.73, 103.19) * mm, "construction": true});
            skArc(sketch, "E98.4", {"start": v(215.58, 18.42) * mm, "mid": v(220.66, 13.33) * mm, "end": v(215.58, 8.25) * mm, "construction": true});
            skArc(sketch, "E98.5", {"start": v(181.3, 8.25) * mm, "mid": v(176.21, 13.33) * mm, "end": v(181.3, 18.41) * mm, "construction": true});
            skArc(sketch, "E99.0", {"start": v(342.65, 233.04) * mm, "mid": v(347.73, 227.96) * mm, "end": v(342.65, 222.88) * mm, "construction": true});
            skArc(sketch, "E99.1", {"start": v(308.36, 222.88) * mm, "mid": v(303.28, 227.96) * mm, "end": v(308.36, 233.04) * mm, "construction": true});
            skArc(sketch, "E99.2", {"start": v(388.81, 103.5) * mm, "mid": v(383.73, 98.42) * mm, "end": v(378.65, 103.5) * mm, "construction": true});
            skArc(sketch, "E99.3", {"start": v(378.65, 137.8) * mm, "mid": v(383.73, 142.88) * mm, "end": v(388.81, 137.8) * mm, "construction": true});
            skArc(sketch, "E99.4", {"start": v(342.65, 18.42) * mm, "mid": v(347.73, 13.34) * mm, "end": v(342.65, 8.25) * mm, "construction": true});
            skArc(sketch, "E99.5", {"start": v(308.36, 8.26) * mm, "mid": v(303.28, 13.34) * mm, "end": v(308.36, 18.42) * mm, "construction": true});
            skLineSegment(sketch, "E100.0", {"start": v(15.68, 220.66) * mm, "end": v(15.68, 20.64) * mm, "construction": true});
            skCircle(sketch, "E101", {"center": v(11.87, 175.9) * mm, "radius": 4.57 * mm});
            skPoint(sketch, "E102", {"position": v(16.45, 175.9) * mm});
            skCircle(sketch, "E103", {"center": v(44.07, 229.24) * mm, "radius": 4.57 * mm});
            skLineSegment(sketch, "E104", {"start": v(11.87, 175.9) * mm, "end": v(13.14, 175.9) * mm, "construction": true});
            skLineSegment(sketch, "E105", {"start": v(44.07, 229.24) * mm, "end": v(44.07, 227.97) * mm});
            skLineSegment(sketch, "E106", {"start": v(129.6, 120.65) * mm, "end": v(15.68, 120.65) * mm, "construction": true});
            skLineSegment(sketch, "E107", {"start": v(71.37, 227.97) * mm, "end": v(71.37, 13.33) * mm, "construction": true});
            skLineSegment(sketch, "E108.bottom", {"start": v(13.14, 182.25) * mm, "end": v(19.75, 182.25) * mm});
            skLineSegment(sketch, "E108.top", {"start": v(13.14, 169.55) * mm, "end": v(19.75, 169.55) * mm});
            skLineSegment(sketch, "E108.left", {"start": v(13.14, 182.25) * mm, "end": v(13.14, 169.55) * mm});
            skLineSegment(sketch, "E108.right", {"start": v(19.75, 182.25) * mm, "end": v(19.75, 169.55) * mm});
            skPoint(sketch, "E109", {"position": v(44.07, 224.66) * mm});
            skLineSegment(sketch, "E110.bottom", {"start": v(37.72, 227.97) * mm, "end": v(50.42, 227.97) * mm});
            skLineSegment(sketch, "E110.top", {"start": v(37.72, 221.36) * mm, "end": v(50.42, 221.36) * mm});
            skLineSegment(sketch, "E110.left", {"start": v(37.72, 227.97) * mm, "end": v(37.72, 221.36) * mm});
            skLineSegment(sketch, "E110.right", {"start": v(50.42, 227.97) * mm, "end": v(50.42, 221.36) * mm});
            skCircle(sketch, "E111.MirrorC", {"center": v(98.68, 229.24) * mm, "radius": 4.57 * mm});
            skLineSegment(sketch, "E112.MirrorCS", {"start": v(105.03, 221.36) * mm, "end": v(92.33, 221.36) * mm});
            skLineSegment(sketch, "E113.MirrorCS", {"start": v(92.33, 227.97) * mm, "end": v(92.33, 221.36) * mm});
            skLineSegment(sketch, "E114.MirrorCS", {"start": v(105.03, 227.97) * mm, "end": v(105.03, 221.36) * mm});
            skLineSegment(sketch, "E115.MirrorCS", {"start": v(105.03, 227.97) * mm, "end": v(92.33, 227.97) * mm});
            skCircle(sketch, "E116.MirrorC", {"center": v(130.87, 175.9) * mm, "radius": 4.57 * mm});
            skLineSegment(sketch, "E117.MirrorCS", {"start": v(129.6, 182.25) * mm, "end": v(129.6, 169.55) * mm});
            skLineSegment(sketch, "E118.MirrorCS", {"start": v(129.6, 182.25) * mm, "end": v(123, 182.25) * mm});
            skLineSegment(sketch, "E119.MirrorCS", {"start": v(123, 182.25) * mm, "end": v(123, 169.55) * mm});
            skLineSegment(sketch, "E120.MirrorCS", {"start": v(129.6, 169.55) * mm, "end": v(123, 169.55) * mm});
            skCircle(sketch, "E121.MirrorC", {"center": v(11.87, 65.4) * mm, "radius": 4.57 * mm});
            skLineSegment(sketch, "E122.MirrorCS", {"start": v(13.14, 59.06) * mm, "end": v(19.75, 59.06) * mm});
            skLineSegment(sketch, "E123.MirrorCS", {"start": v(19.75, 59.06) * mm, "end": v(19.75, 71.76) * mm});
            skLineSegment(sketch, "E124.MirrorCS", {"start": v(13.14, 71.76) * mm, "end": v(19.75, 71.76) * mm});
            skLineSegment(sketch, "E125.MirrorCS", {"start": v(13.14, 59.06) * mm, "end": v(13.14, 71.76) * mm});
            skCircle(sketch, "E126.MirrorC", {"center": v(44.07, 12.07) * mm, "radius": 4.57 * mm});
            skLineSegment(sketch, "E127.MirrorCS", {"start": v(37.72, 13.34) * mm, "end": v(37.72, 19.94) * mm});
            skLineSegment(sketch, "E128.MirrorCS", {"start": v(37.72, 19.94) * mm, "end": v(50.42, 19.94) * mm});
            skLineSegment(sketch, "E129.MirrorCS", {"start": v(50.42, 13.34) * mm, "end": v(50.42, 19.94) * mm});
            skLineSegment(sketch, "E130.MirrorCS", {"start": v(37.72, 13.34) * mm, "end": v(50.42, 13.34) * mm});
            skLineSegment(sketch, "E131.MirrorCS", {"start": v(105.03, 13.34) * mm, "end": v(92.33, 13.34) * mm});
            skLineSegment(sketch, "E132.MirrorCS", {"start": v(92.33, 13.34) * mm, "end": v(92.33, 19.94) * mm});
            skLineSegment(sketch, "E133.MirrorCS", {"start": v(105.03, 13.34) * mm, "end": v(105.03, 19.94) * mm});
            skLineSegment(sketch, "E134.MirrorCS", {"start": v(105.03, 19.94) * mm, "end": v(92.33, 19.94) * mm});
            skCircle(sketch, "E135.MirrorC", {"center": v(98.68, 12.07) * mm, "radius": 4.57 * mm});
            skCircle(sketch, "E136.MirrorC", {"center": v(130.87, 65.4) * mm, "radius": 4.57 * mm});
            skLineSegment(sketch, "E137.MirrorCS", {"start": v(129.6, 71.76) * mm, "end": v(123, 71.76) * mm});
            skLineSegment(sketch, "E138.MirrorCS", {"start": v(123, 59.06) * mm, "end": v(123, 71.76) * mm});
            skLineSegment(sketch, "E139.MirrorCS", {"start": v(129.6, 59.06) * mm, "end": v(129.6, 71.76) * mm});
            skLineSegment(sketch, "E140.MirrorCS", {"start": v(129.6, 59.06) * mm, "end": v(123, 59.06) * mm});
            skLineSegment(sketch, "E141.1.0.0", {"start": v(140.2, 71.76) * mm, "end": v(146.81, 71.76) * mm});
            skLineSegment(sketch, "E141.1.0.1", {"start": v(146.81, 59.06) * mm, "end": v(146.81, 71.76) * mm});
            skLineSegment(sketch, "E141.1.0.2", {"start": v(140.2, 59.06) * mm, "end": v(146.81, 59.06) * mm});
            skLineSegment(sketch, "E141.1.0.3", {"start": v(140.2, 59.06) * mm, "end": v(140.2, 71.76) * mm});
            skCircle(sketch, "E141.1.0.4", {"center": v(138.94, 65.4) * mm, "radius": 4.57 * mm});
            skLineSegment(sketch, "E141.1.0.5", {"start": v(177.48, 13.34) * mm, "end": v(177.48, 19.94) * mm});
            skLineSegment(sketch, "E141.1.0.6", {"start": v(164.78, 13.34) * mm, "end": v(164.78, 19.94) * mm});
            skLineSegment(sketch, "E141.1.0.7", {"start": v(164.78, 19.94) * mm, "end": v(177.48, 19.94) * mm});
            skCircle(sketch, "E141.1.0.8", {"center": v(171.13, 12.07) * mm, "radius": 4.57 * mm});
            skLineSegment(sketch, "E141.1.0.9", {"start": v(164.78, 13.34) * mm, "end": v(177.48, 13.34) * mm});
            skLineSegment(sketch, "E141.1.0.10", {"start": v(256.67, 71.76) * mm, "end": v(250.06, 71.76) * mm});
            skCircle(sketch, "E141.1.0.11", {"center": v(257.94, 65.4) * mm, "radius": 4.57 * mm});
            skLineSegment(sketch, "E141.1.0.12", {"start": v(250.06, 59.06) * mm, "end": v(250.06, 71.76) * mm});
            skLineSegment(sketch, "E141.1.0.13", {"start": v(256.67, 59.06) * mm, "end": v(250.06, 59.06) * mm});
            skLineSegment(sketch, "E141.1.0.14", {"start": v(256.67, 59.06) * mm, "end": v(256.67, 71.76) * mm});
            skLineSegment(sketch, "E141.1.0.15", {"start": v(219.4, 13.34) * mm, "end": v(219.4, 19.94) * mm});
            skLineSegment(sketch, "E141.1.0.16", {"start": v(232.1, 19.94) * mm, "end": v(219.4, 19.94) * mm});
            skCircle(sketch, "E141.1.0.17", {"center": v(225.74, 12.07) * mm, "radius": 4.57 * mm});
            skLineSegment(sketch, "E141.1.0.18", {"start": v(232.1, 13.34) * mm, "end": v(232.1, 19.94) * mm});
            skLineSegment(sketch, "E141.1.0.19", {"start": v(232.1, 13.34) * mm, "end": v(219.4, 13.34) * mm});
            skLineSegment(sketch, "E141.1.0.20", {"start": v(256.67, 182.25) * mm, "end": v(250.06, 182.25) * mm});
            skCircle(sketch, "E141.1.0.21", {"center": v(257.94, 175.9) * mm, "radius": 4.57 * mm});
            skLineSegment(sketch, "E141.1.0.22", {"start": v(256.67, 182.25) * mm, "end": v(256.67, 169.55) * mm});
            skLineSegment(sketch, "E141.1.0.23", {"start": v(256.67, 169.55) * mm, "end": v(250.06, 169.55) * mm});
            skLineSegment(sketch, "E141.1.0.24", {"start": v(250.06, 182.25) * mm, "end": v(250.06, 169.55) * mm});
            skCircle(sketch, "E141.1.0.25", {"center": v(225.74, 229.24) * mm, "radius": 4.57 * mm});
            skLineSegment(sketch, "E141.1.0.26", {"start": v(232.1, 227.97) * mm, "end": v(219.4, 227.97) * mm});
            skLineSegment(sketch, "E141.1.0.27", {"start": v(232.1, 221.36) * mm, "end": v(219.4, 221.36) * mm});
            skLineSegment(sketch, "E141.1.0.28", {"start": v(219.4, 227.97) * mm, "end": v(219.4, 221.36) * mm});
            skLineSegment(sketch, "E141.1.0.29", {"start": v(232.1, 227.97) * mm, "end": v(232.1, 221.36) * mm});
            skCircle(sketch, "E141.1.0.30", {"center": v(171.13, 229.24) * mm, "radius": 4.57 * mm});
            skLineSegment(sketch, "E141.1.0.31", {"start": v(164.78, 227.97) * mm, "end": v(164.78, 221.36) * mm});
            skLineSegment(sketch, "E141.1.0.32", {"start": v(164.78, 221.36) * mm, "end": v(177.48, 221.36) * mm});
            skLineSegment(sketch, "E141.1.0.33", {"start": v(177.48, 227.97) * mm, "end": v(177.48, 221.36) * mm});
            skLineSegment(sketch, "E141.1.0.34", {"start": v(164.78, 227.97) * mm, "end": v(177.48, 227.97) * mm});
            skLineSegment(sketch, "E141.1.0.35", {"start": v(140.2, 182.25) * mm, "end": v(146.81, 182.25) * mm});
            skLineSegment(sketch, "E141.1.0.36", {"start": v(146.81, 182.25) * mm, "end": v(146.81, 169.55) * mm});
            skLineSegment(sketch, "E141.1.0.37", {"start": v(140.2, 169.55) * mm, "end": v(146.81, 169.55) * mm});
            skCircle(sketch, "E141.1.0.38", {"center": v(138.94, 175.9) * mm, "radius": 4.57 * mm});
            skLineSegment(sketch, "E141.1.0.39", {"start": v(140.2, 182.25) * mm, "end": v(140.2, 169.55) * mm});
            skLineSegment(sketch, "E141.2.0.0", {"start": v(267.27, 71.76) * mm, "end": v(273.88, 71.76) * mm});
            skLineSegment(sketch, "E141.2.0.1", {"start": v(273.88, 59.06) * mm, "end": v(273.88, 71.76) * mm});
            skLineSegment(sketch, "E141.2.0.2", {"start": v(267.27, 59.06) * mm, "end": v(273.88, 59.06) * mm});
            skLineSegment(sketch, "E141.2.0.3", {"start": v(267.27, 59.06) * mm, "end": v(267.27, 71.76) * mm});
            skCircle(sketch, "E141.2.0.4", {"center": v(266, 65.4) * mm, "radius": 4.57 * mm});
            skLineSegment(sketch, "E141.2.0.5", {"start": v(304.55, 13.34) * mm, "end": v(304.55, 19.94) * mm});
            skLineSegment(sketch, "E141.2.0.6", {"start": v(291.85, 13.34) * mm, "end": v(291.85, 19.94) * mm});
            skLineSegment(sketch, "E141.2.0.7", {"start": v(291.85, 19.94) * mm, "end": v(304.55, 19.94) * mm});
            skCircle(sketch, "E141.2.0.8", {"center": v(298.2, 12.07) * mm, "radius": 4.57 * mm});
            skLineSegment(sketch, "E141.2.0.9", {"start": v(291.85, 13.34) * mm, "end": v(304.55, 13.34) * mm});
            skLineSegment(sketch, "E141.2.0.10", {"start": v(383.73, 71.76) * mm, "end": v(377.13, 71.76) * mm});
            skCircle(sketch, "E141.2.0.11", {"center": v(385, 65.4) * mm, "radius": 4.57 * mm});
            skLineSegment(sketch, "E141.2.0.12", {"start": v(377.13, 59.06) * mm, "end": v(377.13, 71.76) * mm});
            skLineSegment(sketch, "E141.2.0.13", {"start": v(383.73, 59.06) * mm, "end": v(377.13, 59.06) * mm});
            skLineSegment(sketch, "E141.2.0.14", {"start": v(383.73, 59.06) * mm, "end": v(383.73, 71.76) * mm});
            skLineSegment(sketch, "E141.2.0.15", {"start": v(346.46, 13.34) * mm, "end": v(346.46, 19.94) * mm});
            skLineSegment(sketch, "E141.2.0.16", {"start": v(359.16, 19.94) * mm, "end": v(346.46, 19.94) * mm});
            skCircle(sketch, "E141.2.0.17", {"center": v(352.8, 12.07) * mm, "radius": 4.57 * mm});
            skLineSegment(sketch, "E141.2.0.18", {"start": v(359.16, 13.34) * mm, "end": v(359.16, 19.94) * mm});
            skLineSegment(sketch, "E141.2.0.19", {"start": v(359.16, 13.34) * mm, "end": v(346.46, 13.34) * mm});
            skLineSegment(sketch, "E141.2.0.20", {"start": v(383.73, 182.25) * mm, "end": v(377.13, 182.25) * mm});
            skCircle(sketch, "E141.2.0.21", {"center": v(385, 175.9) * mm, "radius": 4.57 * mm});
            skLineSegment(sketch, "E141.2.0.22", {"start": v(383.73, 182.25) * mm, "end": v(383.73, 169.55) * mm});
            skLineSegment(sketch, "E141.2.0.23", {"start": v(383.73, 169.55) * mm, "end": v(377.13, 169.55) * mm});
            skLineSegment(sketch, "E141.2.0.24", {"start": v(377.13, 182.25) * mm, "end": v(377.13, 169.55) * mm});
            skCircle(sketch, "E141.2.0.25", {"center": v(352.8, 229.24) * mm, "radius": 4.57 * mm});
            skLineSegment(sketch, "E141.2.0.26", {"start": v(359.16, 227.97) * mm, "end": v(346.46, 227.97) * mm});
            skLineSegment(sketch, "E141.2.0.27", {"start": v(359.16, 221.36) * mm, "end": v(346.46, 221.36) * mm});
            skLineSegment(sketch, "E141.2.0.28", {"start": v(346.46, 227.97) * mm, "end": v(346.46, 221.36) * mm});
            skLineSegment(sketch, "E141.2.0.29", {"start": v(359.16, 227.97) * mm, "end": v(359.16, 221.36) * mm});
            skCircle(sketch, "E141.2.0.30", {"center": v(298.2, 229.24) * mm, "radius": 4.57 * mm});
            skLineSegment(sketch, "E141.2.0.31", {"start": v(291.85, 227.97) * mm, "end": v(291.85, 221.36) * mm});
            skLineSegment(sketch, "E141.2.0.32", {"start": v(291.85, 221.36) * mm, "end": v(304.55, 221.36) * mm});
            skLineSegment(sketch, "E141.2.0.33", {"start": v(304.55, 227.97) * mm, "end": v(304.55, 221.36) * mm});
            skLineSegment(sketch, "E141.2.0.34", {"start": v(291.85, 227.97) * mm, "end": v(304.55, 227.97) * mm});
            skLineSegment(sketch, "E141.2.0.35", {"start": v(267.27, 182.25) * mm, "end": v(273.88, 182.25) * mm});
            skLineSegment(sketch, "E141.2.0.36", {"start": v(273.88, 182.25) * mm, "end": v(273.88, 169.55) * mm});
            skLineSegment(sketch, "E141.2.0.37", {"start": v(267.27, 169.55) * mm, "end": v(273.88, 169.55) * mm});
            skCircle(sketch, "E141.2.0.38", {"center": v(266, 175.9) * mm, "radius": 4.57 * mm});
            skLineSegment(sketch, "E141.2.0.39", {"start": v(267.27, 182.25) * mm, "end": v(267.27, 169.55) * mm});
            skLineSegment(sketch, "E141.direction1", {"start": v(13.14, 59.06) * mm, "end": v(140.2, 59.06) * mm, "construction": true});
            skSolve(sketch);
        }
        {
            var Q0;
            Q0=makeQuery(id+"F6.imprint","IMPRINT",FACE,{"disambiguationData":[TD([[makeQuery(id+"F6.imprint","IMPRINT",EDGE,{"derivedFrom":sQuery(id+"F6.wireOp",EDGE,"E28.bottom")}),1.0]])]});
            var Q1;
            Q1=makeQuery(id+"F6.imprint","IMPRINT",FACE,{"disambiguationData":[TD([[makeQuery(id+"F6.imprint","IMPRINT",EDGE,{"derivedFrom":sQuery(id+"F6.wireOp",EDGE,"E29.bottom")}),1.0]])]});
            var Q2;
            Q2=makeQuery(id+"F6.imprint","IMPRINT",FACE,{"disambiguationData":[TD([[makeQuery(id+"F6.imprint","IMPRINT",EDGE,{"derivedFrom":sQuery(id+"F6.wireOp",EDGE,"E30.bottom")}),1.0]])]});
            extrude(context, id + "F16", {"entities" : qUnion([Q0, Q1, Q2]), "operationType" : NewBodyOperationType.ADD, "depth" : 5.08 * mm, "hasDraft" : true, "draftAngle" : 3 * degree, "draftPullDirection" : true});
        }
        {
            var Q0;
            {var subQ0=sQuery(id+"F15.wireOp",EDGE,"E108.left");var subQ1=sQuery(id+"F15.wireOp",EDGE,"E101");var subQ2=makeQuery(id+"F15.imprint","INTERSECT",VERTEX,{"disambiguationData":[OD(0.0)],"derivedFrom":[subQ1,subQ0]});Q0=makeQuery(id+"F15.imprint","IMPRINT",FACE,{"disambiguationData":[TD([[makeQuery(id+"F15.imprint","IMPRINT",EDGE,{"disambiguationData":[TD([[subQ2,-1.0]])],"derivedFrom":subQ1}),1.0]])]});}
            var Q1;
            {var subQ0=sQuery(id+"F15.wireOp",EDGE,"E110.bottom");var subQ4=makeQuery(id+"F15.imprint","IMPRINT",VERTEX,{"derivedFrom":subQ0});Q1=makeQuery(id+"F15.imprint","IMPRINT",FACE,{"disambiguationData":[TD([[makeQuery(id+"F15.imprint","IMPRINT",EDGE,{"disambiguationData":[TD([[subQ4,1.0]])],"derivedFrom":subQ0}),1.0]])]});}
            var Q2;
            {var subQ0=sQuery(id+"F15.wireOp",EDGE,"E115.MirrorCS");var subQ1=sQuery(id+"F15.wireOp",EDGE,"E111.MirrorC");var subQ2=makeQuery(id+"F15.imprint","INTERSECT",VERTEX,{"disambiguationData":[OD(0.0)],"derivedFrom":[subQ1,subQ0]});Q2=makeQuery(id+"F15.imprint","IMPRINT",FACE,{"disambiguationData":[TD([[makeQuery(id+"F15.imprint","IMPRINT",EDGE,{"disambiguationData":[TD([[subQ2,1.0]])],"derivedFrom":subQ1}),-1.0]])]});}
            var Q3;
            {var subQ0=sQuery(id+"F15.wireOp",EDGE,"E125.MirrorCS");var subQ1=sQuery(id+"F15.wireOp",EDGE,"E121.MirrorC");var subQ2=makeQuery(id+"F15.imprint","INTERSECT",VERTEX,{"disambiguationData":[OD(0.0)],"derivedFrom":[subQ1,subQ0]});Q3=makeQuery(id+"F15.imprint","IMPRINT",FACE,{"disambiguationData":[TD([[makeQuery(id+"F15.imprint","IMPRINT",EDGE,{"disambiguationData":[TD([[subQ2,-1.0]])],"derivedFrom":subQ1}),-1.0]])]});}
            var Q4;
            {var subQ0=sQuery(id+"F15.wireOp",EDGE,"E130.MirrorCS");var subQ1=sQuery(id+"F15.wireOp",EDGE,"E126.MirrorC");var subQ2=makeQuery(id+"F15.imprint","INTERSECT",VERTEX,{"disambiguationData":[OD(0.0)],"derivedFrom":[subQ1,subQ0]});Q4=makeQuery(id+"F15.imprint","IMPRINT",FACE,{"disambiguationData":[TD([[makeQuery(id+"F15.imprint","IMPRINT",EDGE,{"disambiguationData":[TD([[subQ2,1.0]])],"derivedFrom":subQ1}),-1.0]])]});}
            var Q5;
            {var subQ0=sQuery(id+"F15.wireOp",EDGE,"E135.MirrorC");var subQ1=sQuery(id+"F15.wireOp",EDGE,"E131.MirrorCS");var subQ2=makeQuery(id+"F15.imprint","INTERSECT",VERTEX,{"disambiguationData":[OD(0.0)],"derivedFrom":[subQ1,subQ0]});Q5=makeQuery(id+"F15.imprint","IMPRINT",FACE,{"disambiguationData":[TD([[makeQuery(id+"F15.imprint","IMPRINT",EDGE,{"disambiguationData":[TD([[subQ2,-1.0]])],"derivedFrom":subQ1}),1.0]])]});}
            var Q6;
            {var subQ0=sQuery(id+"F15.wireOp",EDGE,"E141.1.0.9");var subQ1=sQuery(id+"F15.wireOp",EDGE,"E141.1.0.8");var subQ2=makeQuery(id+"F15.imprint","INTERSECT",VERTEX,{"disambiguationData":[OD(0.0)],"derivedFrom":[subQ1,subQ0]});Q6=makeQuery(id+"F15.imprint","IMPRINT",FACE,{"disambiguationData":[TD([[makeQuery(id+"F15.imprint","IMPRINT",EDGE,{"disambiguationData":[TD([[subQ2,1.0]])],"derivedFrom":subQ1}),-1.0]])]});}
            var Q7;
            {var subQ0=sQuery(id+"F15.wireOp",EDGE,"E141.1.0.19");var subQ1=sQuery(id+"F15.wireOp",EDGE,"E141.1.0.17");var subQ2=makeQuery(id+"F15.imprint","INTERSECT",VERTEX,{"disambiguationData":[OD(0.0)],"derivedFrom":[subQ1,subQ0]});Q7=makeQuery(id+"F15.imprint","IMPRINT",FACE,{"disambiguationData":[TD([[makeQuery(id+"F15.imprint","IMPRINT",EDGE,{"disambiguationData":[TD([[subQ2,1.0]])],"derivedFrom":subQ1}),1.0]])]});}
            var Q8;
            {var subQ0=sQuery(id+"F15.wireOp",EDGE,"E141.1.0.26");var subQ1=sQuery(id+"F15.wireOp",EDGE,"E141.1.0.25");var subQ2=makeQuery(id+"F15.imprint","INTERSECT",VERTEX,{"disambiguationData":[OD(0.0)],"derivedFrom":[subQ1,subQ0]});Q8=makeQuery(id+"F15.imprint","IMPRINT",FACE,{"disambiguationData":[TD([[makeQuery(id+"F15.imprint","IMPRINT",EDGE,{"disambiguationData":[TD([[subQ2,1.0]])],"derivedFrom":subQ1}),-1.0]])]});}
            var Q9;
            {var subQ0=sQuery(id+"F15.wireOp",EDGE,"E141.1.0.34");var subQ1=sQuery(id+"F15.wireOp",EDGE,"E141.1.0.30");var subQ2=makeQuery(id+"F15.imprint","INTERSECT",VERTEX,{"disambiguationData":[OD(0.0)],"derivedFrom":[subQ1,subQ0]});Q9=makeQuery(id+"F15.imprint","IMPRINT",FACE,{"disambiguationData":[TD([[makeQuery(id+"F15.imprint","IMPRINT",EDGE,{"disambiguationData":[TD([[subQ2,1.0]])],"derivedFrom":subQ1}),1.0]])]});}
            var Q10;
            {var subQ0=sQuery(id+"F15.wireOp",EDGE,"E141.2.0.9");var subQ1=sQuery(id+"F15.wireOp",EDGE,"E141.2.0.8");var subQ2=makeQuery(id+"F15.imprint","INTERSECT",VERTEX,{"disambiguationData":[OD(0.0)],"derivedFrom":[subQ1,subQ0]});Q10=makeQuery(id+"F15.imprint","IMPRINT",FACE,{"disambiguationData":[TD([[makeQuery(id+"F15.imprint","IMPRINT",EDGE,{"disambiguationData":[TD([[subQ2,1.0]])],"derivedFrom":subQ1}),-1.0]])]});}
            var Q11;
            {var subQ0=sQuery(id+"F15.wireOp",EDGE,"E141.2.0.14");var subQ1=sQuery(id+"F15.wireOp",EDGE,"E141.2.0.11");var subQ2=makeQuery(id+"F15.imprint","INTERSECT",VERTEX,{"disambiguationData":[OD(0.0)],"derivedFrom":[subQ1,subQ0]});Q11=makeQuery(id+"F15.imprint","IMPRINT",FACE,{"disambiguationData":[TD([[makeQuery(id+"F15.imprint","IMPRINT",EDGE,{"disambiguationData":[TD([[subQ2,-1.0]])],"derivedFrom":subQ1}),1.0]])]});}
            var Q12;
            {var subQ0=sQuery(id+"F15.wireOp",EDGE,"E141.2.0.19");var subQ1=sQuery(id+"F15.wireOp",EDGE,"E141.2.0.17");var subQ2=makeQuery(id+"F15.imprint","INTERSECT",VERTEX,{"disambiguationData":[OD(0.0)],"derivedFrom":[subQ1,subQ0]});Q12=makeQuery(id+"F15.imprint","IMPRINT",FACE,{"disambiguationData":[TD([[makeQuery(id+"F15.imprint","IMPRINT",EDGE,{"disambiguationData":[TD([[subQ2,1.0]])],"derivedFrom":subQ1}),1.0]])]});}
            var Q13;
            {var subQ0=sQuery(id+"F15.wireOp",EDGE,"E141.2.0.22");var subQ1=sQuery(id+"F15.wireOp",EDGE,"E141.2.0.21");var subQ2=makeQuery(id+"F15.imprint","INTERSECT",VERTEX,{"disambiguationData":[OD(0.0)],"derivedFrom":[subQ1,subQ0]});Q13=makeQuery(id+"F15.imprint","IMPRINT",FACE,{"disambiguationData":[TD([[makeQuery(id+"F15.imprint","IMPRINT",EDGE,{"disambiguationData":[TD([[subQ2,-1.0]])],"derivedFrom":subQ1}),-1.0]])]});}
            var Q14;
            {var subQ0=sQuery(id+"F15.wireOp",EDGE,"E141.2.0.26");var subQ1=sQuery(id+"F15.wireOp",EDGE,"E141.2.0.25");var subQ2=makeQuery(id+"F15.imprint","INTERSECT",VERTEX,{"disambiguationData":[OD(0.0)],"derivedFrom":[subQ1,subQ0]});Q14=makeQuery(id+"F15.imprint","IMPRINT",FACE,{"disambiguationData":[TD([[makeQuery(id+"F15.imprint","IMPRINT",EDGE,{"disambiguationData":[TD([[subQ2,1.0]])],"derivedFrom":subQ1}),-1.0]])]});}
            var Q15;
            {var subQ0=sQuery(id+"F15.wireOp",EDGE,"E141.2.0.34");var subQ1=sQuery(id+"F15.wireOp",EDGE,"E141.2.0.30");var subQ2=makeQuery(id+"F15.imprint","INTERSECT",VERTEX,{"disambiguationData":[OD(0.0)],"derivedFrom":[subQ1,subQ0]});Q15=makeQuery(id+"F15.imprint","IMPRINT",FACE,{"disambiguationData":[TD([[makeQuery(id+"F15.imprint","IMPRINT",EDGE,{"disambiguationData":[TD([[subQ2,1.0]])],"derivedFrom":subQ1}),1.0]])]});}
            var Q16;
            {var subQ0=sQuery(id+"F15.wireOp",EDGE,"E108.left");var subQ1=sQuery(id+"F15.wireOp",EDGE,"E101");var subQ2=makeQuery(id+"F15.imprint","INTERSECT",VERTEX,{"disambiguationData":[OD(0.0)],"derivedFrom":[subQ1,subQ0]});Q16=makeQuery(id+"F15.imprint","IMPRINT",FACE,{"disambiguationData":[TD([[makeQuery(id+"F15.imprint","IMPRINT",EDGE,{"disambiguationData":[TD([[subQ2,1.0]])],"derivedFrom":subQ1}),1.0]])]});}
            var Q17;
            {var subQ0=sQuery(id+"F15.wireOp",EDGE,"E110.bottom");var subQ4=makeQuery(id+"F15.imprint","IMPRINT",VERTEX,{"derivedFrom":subQ0});Q17=makeQuery(id+"F15.imprint","IMPRINT",FACE,{"disambiguationData":[TD([[makeQuery(id+"F15.imprint","IMPRINT",EDGE,{"disambiguationData":[TD([[subQ4,1.0]])],"derivedFrom":subQ0}),-1.0]])]});}
            var Q18;
            {var subQ0=sQuery(id+"F15.wireOp",EDGE,"E115.MirrorCS");var subQ1=sQuery(id+"F15.wireOp",EDGE,"E111.MirrorC");var subQ2=makeQuery(id+"F15.imprint","INTERSECT",VERTEX,{"disambiguationData":[OD(0.0)],"derivedFrom":[subQ1,subQ0]});Q18=makeQuery(id+"F15.imprint","IMPRINT",FACE,{"disambiguationData":[TD([[makeQuery(id+"F15.imprint","IMPRINT",EDGE,{"disambiguationData":[TD([[subQ2,-1.0]])],"derivedFrom":subQ1}),-1.0]])]});}
            var Q19;
            {var subQ0=sQuery(id+"F15.wireOp",EDGE,"E141.1.0.38");var subQ1=sQuery(id+"F15.wireOp",EDGE,"E116.MirrorC");var subQ2=makeQuery(id+"F15.imprint","INTERSECT",VERTEX,{"disambiguationData":[OD(0.0)],"derivedFrom":[subQ1,subQ0]});Q19=makeQuery(id+"F15.imprint","IMPRINT",FACE,{"disambiguationData":[TD([[makeQuery(id+"F15.imprint","IMPRINT",EDGE,{"disambiguationData":[TD([[subQ2,1.0]])],"derivedFrom":subQ1}),-1.0]])]});}
            var Q20;
            {var subQ0=sQuery(id+"F15.wireOp",EDGE,"E141.1.0.38");var subQ1=sQuery(id+"F15.wireOp",EDGE,"E116.MirrorC");var subQ2=makeQuery(id+"F15.imprint","INTERSECT",VERTEX,{"disambiguationData":[OD(0.0)],"derivedFrom":[subQ1,subQ0]});Q20=makeQuery(id+"F15.imprint","IMPRINT",FACE,{"disambiguationData":[TD([[makeQuery(id+"F15.imprint","IMPRINT",EDGE,{"disambiguationData":[TD([[subQ2,-1.0]])],"derivedFrom":subQ1}),1.0]])]});}
            var Q21;
            {var subQ0=sQuery(id+"F15.wireOp",EDGE,"E141.1.0.38");var subQ1=sQuery(id+"F15.wireOp",EDGE,"E116.MirrorC");var subQ2=makeQuery(id+"F15.imprint","INTERSECT",VERTEX,{"disambiguationData":[OD(0.0)],"derivedFrom":[subQ1,subQ0]});Q21=makeQuery(id+"F15.imprint","IMPRINT",FACE,{"disambiguationData":[TD([[makeQuery(id+"F15.imprint","IMPRINT",EDGE,{"disambiguationData":[TD([[subQ2,-1.0]])],"derivedFrom":subQ1}),-1.0]])]});}
            var Q22;
            {var subQ0=sQuery(id+"F15.wireOp",EDGE,"E117.MirrorCS");var subQ1=sQuery(id+"F15.wireOp",EDGE,"E116.MirrorC");var subQ2=makeQuery(id+"F15.imprint","INTERSECT",VERTEX,{"disambiguationData":[OD(0.0)],"derivedFrom":[subQ1,subQ0]});Q22=makeQuery(id+"F15.imprint","IMPRINT",FACE,{"disambiguationData":[TD([[makeQuery(id+"F15.imprint","IMPRINT",EDGE,{"disambiguationData":[TD([[subQ2,1.0]])],"derivedFrom":subQ1}),-1.0]])]});}
            var Q23;
            {var subQ0=sQuery(id+"F15.wireOp",EDGE,"E125.MirrorCS");var subQ1=sQuery(id+"F15.wireOp",EDGE,"E121.MirrorC");var subQ2=makeQuery(id+"F15.imprint","INTERSECT",VERTEX,{"disambiguationData":[OD(0.0)],"derivedFrom":[subQ1,subQ0]});Q23=makeQuery(id+"F15.imprint","IMPRINT",FACE,{"disambiguationData":[TD([[makeQuery(id+"F15.imprint","IMPRINT",EDGE,{"disambiguationData":[TD([[subQ2,1.0]])],"derivedFrom":subQ1}),-1.0]])]});}
            var Q24;
            {var subQ0=sQuery(id+"F15.wireOp",EDGE,"E130.MirrorCS");var subQ1=sQuery(id+"F15.wireOp",EDGE,"E126.MirrorC");var subQ2=makeQuery(id+"F15.imprint","INTERSECT",VERTEX,{"disambiguationData":[OD(0.0)],"derivedFrom":[subQ1,subQ0]});Q24=makeQuery(id+"F15.imprint","IMPRINT",FACE,{"disambiguationData":[TD([[makeQuery(id+"F15.imprint","IMPRINT",EDGE,{"disambiguationData":[TD([[subQ2,-1.0]])],"derivedFrom":subQ1}),-1.0]])]});}
            var Q25;
            {var subQ0=sQuery(id+"F15.wireOp",EDGE,"E135.MirrorC");var subQ1=sQuery(id+"F15.wireOp",EDGE,"E131.MirrorCS");var subQ2=makeQuery(id+"F15.imprint","INTERSECT",VERTEX,{"disambiguationData":[OD(0.0)],"derivedFrom":[subQ1,subQ0]});Q25=makeQuery(id+"F15.imprint","IMPRINT",FACE,{"disambiguationData":[TD([[makeQuery(id+"F15.imprint","IMPRINT",EDGE,{"disambiguationData":[TD([[subQ2,-1.0]])],"derivedFrom":subQ1}),-1.0]])]});}
            var Q26;
            {var subQ0=sQuery(id+"F15.wireOp",EDGE,"E141.1.0.4");var subQ1=sQuery(id+"F15.wireOp",EDGE,"E136.MirrorC");var subQ2=makeQuery(id+"F15.imprint","INTERSECT",VERTEX,{"disambiguationData":[OD(0.0)],"derivedFrom":[subQ1,subQ0]});Q26=makeQuery(id+"F15.imprint","IMPRINT",FACE,{"disambiguationData":[TD([[makeQuery(id+"F15.imprint","IMPRINT",EDGE,{"disambiguationData":[TD([[subQ2,1.0]])],"derivedFrom":subQ1}),1.0]])]});}
            var Q27;
            {var subQ0=sQuery(id+"F15.wireOp",EDGE,"E141.1.0.4");var subQ1=sQuery(id+"F15.wireOp",EDGE,"E136.MirrorC");var subQ2=makeQuery(id+"F15.imprint","INTERSECT",VERTEX,{"disambiguationData":[OD(0.0)],"derivedFrom":[subQ1,subQ0]});Q27=makeQuery(id+"F15.imprint","IMPRINT",FACE,{"disambiguationData":[TD([[makeQuery(id+"F15.imprint","IMPRINT",EDGE,{"disambiguationData":[TD([[subQ2,-1.0]])],"derivedFrom":subQ1}),-1.0]])]});}
            var Q28;
            {var subQ0=sQuery(id+"F15.wireOp",EDGE,"E141.1.0.4");var subQ1=sQuery(id+"F15.wireOp",EDGE,"E136.MirrorC");var subQ2=makeQuery(id+"F15.imprint","INTERSECT",VERTEX,{"disambiguationData":[OD(0.0)],"derivedFrom":[subQ1,subQ0]});Q28=makeQuery(id+"F15.imprint","IMPRINT",FACE,{"disambiguationData":[TD([[makeQuery(id+"F15.imprint","IMPRINT",EDGE,{"disambiguationData":[TD([[subQ2,-1.0]])],"derivedFrom":subQ1}),1.0]])]});}
            var Q29;
            {var subQ0=sQuery(id+"F15.wireOp",EDGE,"E139.MirrorCS");var subQ1=sQuery(id+"F15.wireOp",EDGE,"E136.MirrorC");var subQ2=makeQuery(id+"F15.imprint","INTERSECT",VERTEX,{"disambiguationData":[OD(0.0)],"derivedFrom":[subQ1,subQ0]});Q29=makeQuery(id+"F15.imprint","IMPRINT",FACE,{"disambiguationData":[TD([[makeQuery(id+"F15.imprint","IMPRINT",EDGE,{"disambiguationData":[TD([[subQ2,1.0]])],"derivedFrom":subQ1}),1.0]])]});}
            var Q30;
            {var subQ0=sQuery(id+"F15.wireOp",EDGE,"E141.1.0.4");var subQ1=sQuery(id+"F15.wireOp",EDGE,"E141.1.0.3");var subQ2=makeQuery(id+"F15.imprint","INTERSECT",VERTEX,{"disambiguationData":[OD(0.0)],"derivedFrom":[subQ1,subQ0]});Q30=makeQuery(id+"F15.imprint","IMPRINT",FACE,{"disambiguationData":[TD([[makeQuery(id+"F15.imprint","IMPRINT",EDGE,{"disambiguationData":[TD([[subQ2,-1.0]])],"derivedFrom":subQ1}),-1.0]])]});}
            var Q31;
            {var subQ0=sQuery(id+"F15.wireOp",EDGE,"E141.1.0.9");var subQ1=sQuery(id+"F15.wireOp",EDGE,"E141.1.0.8");var subQ2=makeQuery(id+"F15.imprint","INTERSECT",VERTEX,{"disambiguationData":[OD(0.0)],"derivedFrom":[subQ1,subQ0]});Q31=makeQuery(id+"F15.imprint","IMPRINT",FACE,{"disambiguationData":[TD([[makeQuery(id+"F15.imprint","IMPRINT",EDGE,{"disambiguationData":[TD([[subQ2,-1.0]])],"derivedFrom":subQ1}),-1.0]])]});}
            var Q32;
            {var subQ0=sQuery(id+"F15.wireOp",EDGE,"E141.2.0.4");var subQ1=sQuery(id+"F15.wireOp",EDGE,"E141.1.0.11");var subQ2=makeQuery(id+"F15.imprint","INTERSECT",VERTEX,{"disambiguationData":[OD(0.0)],"derivedFrom":[subQ1,subQ0]});Q32=makeQuery(id+"F15.imprint","IMPRINT",FACE,{"disambiguationData":[TD([[makeQuery(id+"F15.imprint","IMPRINT",EDGE,{"disambiguationData":[TD([[subQ2,1.0]])],"derivedFrom":subQ1}),1.0]])]});}
            var Q33;
            {var subQ0=sQuery(id+"F15.wireOp",EDGE,"E141.2.0.4");var subQ1=sQuery(id+"F15.wireOp",EDGE,"E141.1.0.11");var subQ2=makeQuery(id+"F15.imprint","INTERSECT",VERTEX,{"disambiguationData":[OD(0.0)],"derivedFrom":[subQ1,subQ0]});Q33=makeQuery(id+"F15.imprint","IMPRINT",FACE,{"disambiguationData":[TD([[makeQuery(id+"F15.imprint","IMPRINT",EDGE,{"disambiguationData":[TD([[subQ2,-1.0]])],"derivedFrom":subQ1}),-1.0]])]});}
            var Q34;
            {var subQ0=sQuery(id+"F15.wireOp",EDGE,"E141.2.0.4");var subQ1=sQuery(id+"F15.wireOp",EDGE,"E141.1.0.11");var subQ2=makeQuery(id+"F15.imprint","INTERSECT",VERTEX,{"disambiguationData":[OD(0.0)],"derivedFrom":[subQ1,subQ0]});Q34=makeQuery(id+"F15.imprint","IMPRINT",FACE,{"disambiguationData":[TD([[makeQuery(id+"F15.imprint","IMPRINT",EDGE,{"disambiguationData":[TD([[subQ2,-1.0]])],"derivedFrom":subQ1}),1.0]])]});}
            var Q35;
            {var subQ0=sQuery(id+"F15.wireOp",EDGE,"E141.1.0.14");var subQ1=sQuery(id+"F15.wireOp",EDGE,"E141.1.0.11");var subQ2=makeQuery(id+"F15.imprint","INTERSECT",VERTEX,{"disambiguationData":[OD(0.0)],"derivedFrom":[subQ1,subQ0]});Q35=makeQuery(id+"F15.imprint","IMPRINT",FACE,{"disambiguationData":[TD([[makeQuery(id+"F15.imprint","IMPRINT",EDGE,{"disambiguationData":[TD([[subQ2,1.0]])],"derivedFrom":subQ1}),1.0]])]});}
            var Q36;
            {var subQ0=sQuery(id+"F15.wireOp",EDGE,"E141.1.0.19");var subQ1=sQuery(id+"F15.wireOp",EDGE,"E141.1.0.17");var subQ2=makeQuery(id+"F15.imprint","INTERSECT",VERTEX,{"disambiguationData":[OD(0.0)],"derivedFrom":[subQ1,subQ0]});Q36=makeQuery(id+"F15.imprint","IMPRINT",FACE,{"disambiguationData":[TD([[makeQuery(id+"F15.imprint","IMPRINT",EDGE,{"disambiguationData":[TD([[subQ2,-1.0]])],"derivedFrom":subQ1}),1.0]])]});}
            var Q37;
            {var subQ0=sQuery(id+"F15.wireOp",EDGE,"E141.2.0.38");var subQ1=sQuery(id+"F15.wireOp",EDGE,"E141.1.0.21");var subQ2=makeQuery(id+"F15.imprint","INTERSECT",VERTEX,{"disambiguationData":[OD(0.0)],"derivedFrom":[subQ1,subQ0]});Q37=makeQuery(id+"F15.imprint","IMPRINT",FACE,{"disambiguationData":[TD([[makeQuery(id+"F15.imprint","IMPRINT",EDGE,{"disambiguationData":[TD([[subQ2,1.0]])],"derivedFrom":subQ1}),-1.0]])]});}
            var Q38;
            {var subQ0=sQuery(id+"F15.wireOp",EDGE,"E141.2.0.38");var subQ1=sQuery(id+"F15.wireOp",EDGE,"E141.1.0.21");var subQ2=makeQuery(id+"F15.imprint","INTERSECT",VERTEX,{"disambiguationData":[OD(0.0)],"derivedFrom":[subQ1,subQ0]});Q38=makeQuery(id+"F15.imprint","IMPRINT",FACE,{"disambiguationData":[TD([[makeQuery(id+"F15.imprint","IMPRINT",EDGE,{"disambiguationData":[TD([[subQ2,-1.0]])],"derivedFrom":subQ1}),1.0]])]});}
            var Q39;
            {var subQ0=sQuery(id+"F15.wireOp",EDGE,"E141.2.0.38");var subQ1=sQuery(id+"F15.wireOp",EDGE,"E141.1.0.21");var subQ2=makeQuery(id+"F15.imprint","INTERSECT",VERTEX,{"disambiguationData":[OD(0.0)],"derivedFrom":[subQ1,subQ0]});Q39=makeQuery(id+"F15.imprint","IMPRINT",FACE,{"disambiguationData":[TD([[makeQuery(id+"F15.imprint","IMPRINT",EDGE,{"disambiguationData":[TD([[subQ2,-1.0]])],"derivedFrom":subQ1}),-1.0]])]});}
            var Q40;
            {var subQ0=sQuery(id+"F15.wireOp",EDGE,"E141.1.0.22");var subQ1=sQuery(id+"F15.wireOp",EDGE,"E141.1.0.21");var subQ2=makeQuery(id+"F15.imprint","INTERSECT",VERTEX,{"disambiguationData":[OD(0.0)],"derivedFrom":[subQ1,subQ0]});Q40=makeQuery(id+"F15.imprint","IMPRINT",FACE,{"disambiguationData":[TD([[makeQuery(id+"F15.imprint","IMPRINT",EDGE,{"disambiguationData":[TD([[subQ2,1.0]])],"derivedFrom":subQ1}),-1.0]])]});}
            var Q41;
            {var subQ0=sQuery(id+"F15.wireOp",EDGE,"E141.1.0.26");var subQ1=sQuery(id+"F15.wireOp",EDGE,"E141.1.0.25");var subQ2=makeQuery(id+"F15.imprint","INTERSECT",VERTEX,{"disambiguationData":[OD(0.0)],"derivedFrom":[subQ1,subQ0]});Q41=makeQuery(id+"F15.imprint","IMPRINT",FACE,{"disambiguationData":[TD([[makeQuery(id+"F15.imprint","IMPRINT",EDGE,{"disambiguationData":[TD([[subQ2,-1.0]])],"derivedFrom":subQ1}),-1.0]])]});}
            var Q42;
            {var subQ0=sQuery(id+"F15.wireOp",EDGE,"E141.1.0.34");var subQ1=sQuery(id+"F15.wireOp",EDGE,"E141.1.0.30");var subQ2=makeQuery(id+"F15.imprint","INTERSECT",VERTEX,{"disambiguationData":[OD(0.0)],"derivedFrom":[subQ1,subQ0]});Q42=makeQuery(id+"F15.imprint","IMPRINT",FACE,{"disambiguationData":[TD([[makeQuery(id+"F15.imprint","IMPRINT",EDGE,{"disambiguationData":[TD([[subQ2,-1.0]])],"derivedFrom":subQ1}),1.0]])]});}
            var Q43;
            {var subQ0=sQuery(id+"F15.wireOp",EDGE,"E141.1.0.39");var subQ1=sQuery(id+"F15.wireOp",EDGE,"E141.1.0.38");var subQ2=makeQuery(id+"F15.imprint","INTERSECT",VERTEX,{"disambiguationData":[OD(0.0)],"derivedFrom":[subQ1,subQ0]});Q43=makeQuery(id+"F15.imprint","IMPRINT",FACE,{"disambiguationData":[TD([[makeQuery(id+"F15.imprint","IMPRINT",EDGE,{"disambiguationData":[TD([[subQ2,1.0]])],"derivedFrom":subQ1}),1.0]])]});}
            var Q44;
            {var subQ0=sQuery(id+"F15.wireOp",EDGE,"E141.2.0.4");var subQ1=sQuery(id+"F15.wireOp",EDGE,"E141.2.0.3");var subQ2=makeQuery(id+"F15.imprint","INTERSECT",VERTEX,{"disambiguationData":[OD(0.0)],"derivedFrom":[subQ1,subQ0]});Q44=makeQuery(id+"F15.imprint","IMPRINT",FACE,{"disambiguationData":[TD([[makeQuery(id+"F15.imprint","IMPRINT",EDGE,{"disambiguationData":[TD([[subQ2,-1.0]])],"derivedFrom":subQ1}),-1.0]])]});}
            var Q45;
            {var subQ0=sQuery(id+"F15.wireOp",EDGE,"E141.2.0.9");var subQ1=sQuery(id+"F15.wireOp",EDGE,"E141.2.0.8");var subQ2=makeQuery(id+"F15.imprint","INTERSECT",VERTEX,{"disambiguationData":[OD(0.0)],"derivedFrom":[subQ1,subQ0]});Q45=makeQuery(id+"F15.imprint","IMPRINT",FACE,{"disambiguationData":[TD([[makeQuery(id+"F15.imprint","IMPRINT",EDGE,{"disambiguationData":[TD([[subQ2,-1.0]])],"derivedFrom":subQ1}),-1.0]])]});}
            var Q46;
            {var subQ0=sQuery(id+"F15.wireOp",EDGE,"E141.2.0.14");var subQ1=sQuery(id+"F15.wireOp",EDGE,"E141.2.0.11");var subQ2=makeQuery(id+"F15.imprint","INTERSECT",VERTEX,{"disambiguationData":[OD(0.0)],"derivedFrom":[subQ1,subQ0]});Q46=makeQuery(id+"F15.imprint","IMPRINT",FACE,{"disambiguationData":[TD([[makeQuery(id+"F15.imprint","IMPRINT",EDGE,{"disambiguationData":[TD([[subQ2,1.0]])],"derivedFrom":subQ1}),1.0]])]});}
            var Q47;
            {var subQ0=sQuery(id+"F15.wireOp",EDGE,"E141.2.0.19");var subQ1=sQuery(id+"F15.wireOp",EDGE,"E141.2.0.17");var subQ2=makeQuery(id+"F15.imprint","INTERSECT",VERTEX,{"disambiguationData":[OD(0.0)],"derivedFrom":[subQ1,subQ0]});Q47=makeQuery(id+"F15.imprint","IMPRINT",FACE,{"disambiguationData":[TD([[makeQuery(id+"F15.imprint","IMPRINT",EDGE,{"disambiguationData":[TD([[subQ2,-1.0]])],"derivedFrom":subQ1}),1.0]])]});}
            var Q48;
            {var subQ0=sQuery(id+"F15.wireOp",EDGE,"E141.2.0.22");var subQ1=sQuery(id+"F15.wireOp",EDGE,"E141.2.0.21");var subQ2=makeQuery(id+"F15.imprint","INTERSECT",VERTEX,{"disambiguationData":[OD(0.0)],"derivedFrom":[subQ1,subQ0]});Q48=makeQuery(id+"F15.imprint","IMPRINT",FACE,{"disambiguationData":[TD([[makeQuery(id+"F15.imprint","IMPRINT",EDGE,{"disambiguationData":[TD([[subQ2,1.0]])],"derivedFrom":subQ1}),-1.0]])]});}
            var Q49;
            {var subQ0=sQuery(id+"F15.wireOp",EDGE,"E141.2.0.26");var subQ1=sQuery(id+"F15.wireOp",EDGE,"E141.2.0.25");var subQ2=makeQuery(id+"F15.imprint","INTERSECT",VERTEX,{"disambiguationData":[OD(0.0)],"derivedFrom":[subQ1,subQ0]});Q49=makeQuery(id+"F15.imprint","IMPRINT",FACE,{"disambiguationData":[TD([[makeQuery(id+"F15.imprint","IMPRINT",EDGE,{"disambiguationData":[TD([[subQ2,-1.0]])],"derivedFrom":subQ1}),-1.0]])]});}
            var Q50;
            {var subQ0=sQuery(id+"F15.wireOp",EDGE,"E141.2.0.34");var subQ1=sQuery(id+"F15.wireOp",EDGE,"E141.2.0.30");var subQ2=makeQuery(id+"F15.imprint","INTERSECT",VERTEX,{"disambiguationData":[OD(0.0)],"derivedFrom":[subQ1,subQ0]});Q50=makeQuery(id+"F15.imprint","IMPRINT",FACE,{"disambiguationData":[TD([[makeQuery(id+"F15.imprint","IMPRINT",EDGE,{"disambiguationData":[TD([[subQ2,-1.0]])],"derivedFrom":subQ1}),1.0]])]});}
            var Q51;
            {var subQ0=sQuery(id+"F15.wireOp",EDGE,"E141.2.0.39");var subQ1=sQuery(id+"F15.wireOp",EDGE,"E141.2.0.38");var subQ2=makeQuery(id+"F15.imprint","INTERSECT",VERTEX,{"disambiguationData":[OD(0.0)],"derivedFrom":[subQ1,subQ0]});Q51=makeQuery(id+"F15.imprint","IMPRINT",FACE,{"disambiguationData":[TD([[makeQuery(id+"F15.imprint","IMPRINT",EDGE,{"disambiguationData":[TD([[subQ2,1.0]])],"derivedFrom":subQ1}),1.0]])]});}
            var Q52;
            Q52=makeQuery(id+"F14.boolean.opBoolean","MERGE",FACE,{"derivedFrom":[makeQuery(id+"F9.boolean.opBoolean","COPY",FACE,{"derivedFrom":makeQuery(id+"F9.opExtrude","CAP_FACE",FACE,{"disambiguationData":[OSD([sQuery(id+"F5.wireOp",EDGE,"E22.0"),sQuery(id+"F5.wireOp",EDGE,"E22.1"),sQuery(id+"F5.wireOp",EDGE,"E22.2"),sQuery(id+"F5.wireOp",EDGE,"E22.3"),sQuery(id+"F5.wireOp",EDGE,"E22.4"),sQuery(id+"F5.wireOp",EDGE,"E22.5"),sQuery(id+"F5.wireOp",EDGE,"E22.6"),sQuery(id+"F5.wireOp",EDGE,"E22.7")])],"isStart":true})}),makeQuery(id+"F9.boolean.opBoolean","COPY",FACE,{"derivedFrom":makeQuery(id+"F9.opExtrude","CAP_FACE",FACE,{"disambiguationData":[OSD([sQuery(id+"F5.wireOp",EDGE,"E23.0"),sQuery(id+"F5.wireOp",EDGE,"E23.1"),sQuery(id+"F5.wireOp",EDGE,"E23.2"),sQuery(id+"F5.wireOp",EDGE,"E23.3"),sQuery(id+"F5.wireOp",EDGE,"E23.4"),sQuery(id+"F5.wireOp",EDGE,"E23.5"),sQuery(id+"F5.wireOp",EDGE,"E23.6"),sQuery(id+"F5.wireOp",EDGE,"E23.7")])],"isStart":true})}),makeQuery(id+"F9.boolean.opBoolean","COPY",FACE,{"derivedFrom":makeQuery(id+"F9.opExtrude","CAP_FACE",FACE,{"disambiguationData":[OSD([sQuery(id+"F5.wireOp",EDGE,"E24.0"),sQuery(id+"F5.wireOp",EDGE,"E24.1"),sQuery(id+"F5.wireOp",EDGE,"E24.2"),sQuery(id+"F5.wireOp",EDGE,"E24.3"),sQuery(id+"F5.wireOp",EDGE,"E24.4"),sQuery(id+"F5.wireOp",EDGE,"E24.5"),sQuery(id+"F5.wireOp",EDGE,"E24.6"),sQuery(id+"F5.wireOp",EDGE,"E24.7")])],"isStart":true})}),makeQuery(id+"F14.opExtrude","SWEPT_FACE",FACE,{"disambiguationData":[OSD([sQuery(id+"F11.wireOp",EDGE,"E86")])]})]});
            extrude(context, id + "F17", {"entities" : qUnion([Q0, Q1, Q2, Q3, Q4, Q5, Q6, Q7, Q8, Q9, Q10, Q11, Q12, Q13, Q14, Q15, Q16, Q17, Q18, Q19, Q20, Q21, Q22, Q23, Q24, Q25, Q26, Q27, Q28, Q29, Q30, Q31, Q32, Q33, Q34, Q35, Q36, Q37, Q38, Q39, Q40, Q41, Q42, Q43, Q44, Q45, Q46, Q47, Q48, Q49, Q50, Q51]), "operationType" : NewBodyOperationType.ADD, "endBound" : BoundingType.UP_TO_SURFACE, "oppositeDirection" : true, "endBoundEntityFace" : qUnion([Q52]), "depth" : 25.4 * mm});
        }
        {
            var Q0;
            {var subQ1=sQuery(id+"F15.wireOp",EDGE,"E108.bottom");Q0=makeQuery(id+"F15.imprint","IMPRINT",FACE,{"disambiguationData":[TD([[makeQuery(id+"F15.imprint","IMPRINT",EDGE,{"derivedFrom":subQ1}),-1.0]])]});}
            var Q1;
            Q1=makeQuery(id+"F15.imprint","IMPRINT",FACE,{"disambiguationData":[TD([[makeQuery(id+"F15.imprint","IMPRINT",EDGE,{"derivedFrom":sQuery(id+"F15.wireOp",EDGE,"E110.top")}),1.0]])]});
            var Q2;
            Q2=makeQuery(id+"F15.imprint","IMPRINT",FACE,{"disambiguationData":[TD([[makeQuery(id+"F15.imprint","IMPRINT",EDGE,{"derivedFrom":sQuery(id+"F15.wireOp",EDGE,"E112.MirrorCS")}),-1.0]])]});
            var Q3;
            {var subQ0=sQuery(id+"F15.wireOp",EDGE,"E118.MirrorCS");Q3=makeQuery(id+"F15.imprint","IMPRINT",FACE,{"disambiguationData":[TD([[makeQuery(id+"F15.imprint","IMPRINT",EDGE,{"derivedFrom":subQ0}),1.0]])]});}
            var Q4;
            {var subQ0=sQuery(id+"F15.wireOp",EDGE,"E122.MirrorCS");Q4=makeQuery(id+"F15.imprint","IMPRINT",FACE,{"disambiguationData":[TD([[makeQuery(id+"F15.imprint","IMPRINT",EDGE,{"derivedFrom":subQ0}),1.0]])]});}
            var Q5;
            {var subQ1=sQuery(id+"F15.wireOp",EDGE,"E127.MirrorCS");Q5=makeQuery(id+"F15.imprint","IMPRINT",FACE,{"disambiguationData":[TD([[makeQuery(id+"F15.imprint","IMPRINT",EDGE,{"derivedFrom":subQ1}),-1.0]])]});}
            var Q6;
            {var subQ1=sQuery(id+"F15.wireOp",EDGE,"E132.MirrorCS");Q6=makeQuery(id+"F15.imprint","IMPRINT",FACE,{"disambiguationData":[TD([[makeQuery(id+"F15.imprint","IMPRINT",EDGE,{"derivedFrom":subQ1}),-1.0]])]});}
            var Q7;
            {var subQ0=sQuery(id+"F15.wireOp",EDGE,"E137.MirrorCS");Q7=makeQuery(id+"F15.imprint","IMPRINT",FACE,{"disambiguationData":[TD([[makeQuery(id+"F15.imprint","IMPRINT",EDGE,{"derivedFrom":subQ0}),1.0]])]});}
            var Q8;
            {var subQ4=sQuery(id+"F15.wireOp",EDGE,"E141.1.0.0");Q8=makeQuery(id+"F15.imprint","IMPRINT",FACE,{"disambiguationData":[TD([[makeQuery(id+"F15.imprint","IMPRINT",EDGE,{"derivedFrom":subQ4}),-1.0]])]});}
            var Q9;
            {var subQ5=sQuery(id+"F15.wireOp",EDGE,"E141.1.0.5");Q9=makeQuery(id+"F15.imprint","IMPRINT",FACE,{"disambiguationData":[TD([[makeQuery(id+"F15.imprint","IMPRINT",EDGE,{"derivedFrom":subQ5}),1.0]])]});}
            var Q10;
            {var subQ1=sQuery(id+"F15.wireOp",EDGE,"E141.1.0.10");Q10=makeQuery(id+"F15.imprint","IMPRINT",FACE,{"disambiguationData":[TD([[makeQuery(id+"F15.imprint","IMPRINT",EDGE,{"derivedFrom":subQ1}),1.0]])]});}
            var Q11;
            {var subQ5=sQuery(id+"F15.wireOp",EDGE,"E141.1.0.15");Q11=makeQuery(id+"F15.imprint","IMPRINT",FACE,{"disambiguationData":[TD([[makeQuery(id+"F15.imprint","IMPRINT",EDGE,{"derivedFrom":subQ5}),-1.0]])]});}
            var Q12;
            {var subQ1=sQuery(id+"F15.wireOp",EDGE,"E141.1.0.20");Q12=makeQuery(id+"F15.imprint","IMPRINT",FACE,{"disambiguationData":[TD([[makeQuery(id+"F15.imprint","IMPRINT",EDGE,{"derivedFrom":subQ1}),1.0]])]});}
            var Q13;
            Q13=makeQuery(id+"F15.imprint","IMPRINT",FACE,{"disambiguationData":[TD([[makeQuery(id+"F15.imprint","IMPRINT",EDGE,{"derivedFrom":sQuery(id+"F15.wireOp",EDGE,"E141.1.0.27")}),-1.0]])]});
            var Q14;
            {var subQ1=sQuery(id+"F15.wireOp",EDGE,"E141.1.0.31");Q14=makeQuery(id+"F15.imprint","IMPRINT",FACE,{"disambiguationData":[TD([[makeQuery(id+"F15.imprint","IMPRINT",EDGE,{"derivedFrom":subQ1}),1.0]])]});}
            var Q15;
            {var subQ5=sQuery(id+"F15.wireOp",EDGE,"E141.1.0.35");Q15=makeQuery(id+"F15.imprint","IMPRINT",FACE,{"disambiguationData":[TD([[makeQuery(id+"F15.imprint","IMPRINT",EDGE,{"derivedFrom":subQ5}),-1.0]])]});}
            var Q16;
            {var subQ5=sQuery(id+"F15.wireOp",EDGE,"E141.2.0.0");Q16=makeQuery(id+"F15.imprint","IMPRINT",FACE,{"disambiguationData":[TD([[makeQuery(id+"F15.imprint","IMPRINT",EDGE,{"derivedFrom":subQ5}),-1.0]])]});}
            var Q17;
            {var subQ4=sQuery(id+"F15.wireOp",EDGE,"E141.2.0.5");Q17=makeQuery(id+"F15.imprint","IMPRINT",FACE,{"disambiguationData":[TD([[makeQuery(id+"F15.imprint","IMPRINT",EDGE,{"derivedFrom":subQ4}),1.0]])]});}
            var Q18;
            {var subQ5=sQuery(id+"F15.wireOp",EDGE,"E141.2.0.10");Q18=makeQuery(id+"F15.imprint","IMPRINT",FACE,{"disambiguationData":[TD([[makeQuery(id+"F15.imprint","IMPRINT",EDGE,{"derivedFrom":subQ5}),1.0]])]});}
            var Q19;
            {var subQ5=sQuery(id+"F15.wireOp",EDGE,"E141.2.0.15");Q19=makeQuery(id+"F15.imprint","IMPRINT",FACE,{"disambiguationData":[TD([[makeQuery(id+"F15.imprint","IMPRINT",EDGE,{"derivedFrom":subQ5}),-1.0]])]});}
            var Q20;
            {var subQ5=sQuery(id+"F15.wireOp",EDGE,"E141.2.0.20");Q20=makeQuery(id+"F15.imprint","IMPRINT",FACE,{"disambiguationData":[TD([[makeQuery(id+"F15.imprint","IMPRINT",EDGE,{"derivedFrom":subQ5}),1.0]])]});}
            var Q21;
            Q21=makeQuery(id+"F15.imprint","IMPRINT",FACE,{"disambiguationData":[TD([[makeQuery(id+"F15.imprint","IMPRINT",EDGE,{"derivedFrom":sQuery(id+"F15.wireOp",EDGE,"E141.2.0.27")}),-1.0]])]});
            var Q22;
            {var subQ1=sQuery(id+"F15.wireOp",EDGE,"E141.2.0.31");Q22=makeQuery(id+"F15.imprint","IMPRINT",FACE,{"disambiguationData":[TD([[makeQuery(id+"F15.imprint","IMPRINT",EDGE,{"derivedFrom":subQ1}),1.0]])]});}
            var Q23;
            {var subQ5=sQuery(id+"F15.wireOp",EDGE,"E141.2.0.35");Q23=makeQuery(id+"F15.imprint","IMPRINT",FACE,{"disambiguationData":[TD([[makeQuery(id+"F15.imprint","IMPRINT",EDGE,{"derivedFrom":subQ5}),-1.0]])]});}
            var Q24;
            {var subQ0=sQuery(id+"F15.wireOp",EDGE,"E108.left");var subQ1=sQuery(id+"F15.wireOp",EDGE,"E101");var subQ2=makeQuery(id+"F15.imprint","INTERSECT",VERTEX,{"disambiguationData":[OD(0.0)],"derivedFrom":[subQ1,subQ0]});Q24=makeQuery(id+"F15.imprint","IMPRINT",FACE,{"disambiguationData":[TD([[makeQuery(id+"F15.imprint","IMPRINT",EDGE,{"disambiguationData":[TD([[subQ2,1.0]])],"derivedFrom":subQ1}),1.0]])]});}
            var Q25;
            {var subQ0=sQuery(id+"F15.wireOp",EDGE,"E110.bottom");var subQ4=makeQuery(id+"F15.imprint","IMPRINT",VERTEX,{"derivedFrom":subQ0});Q25=makeQuery(id+"F15.imprint","IMPRINT",FACE,{"disambiguationData":[TD([[makeQuery(id+"F15.imprint","IMPRINT",EDGE,{"disambiguationData":[TD([[subQ4,1.0]])],"derivedFrom":subQ0}),-1.0]])]});}
            var Q26;
            {var subQ0=sQuery(id+"F15.wireOp",EDGE,"E115.MirrorCS");var subQ1=sQuery(id+"F15.wireOp",EDGE,"E111.MirrorC");var subQ2=makeQuery(id+"F15.imprint","INTERSECT",VERTEX,{"disambiguationData":[OD(0.0)],"derivedFrom":[subQ1,subQ0]});Q26=makeQuery(id+"F15.imprint","IMPRINT",FACE,{"disambiguationData":[TD([[makeQuery(id+"F15.imprint","IMPRINT",EDGE,{"disambiguationData":[TD([[subQ2,-1.0]])],"derivedFrom":subQ1}),-1.0]])]});}
            var Q27;
            {var subQ0=sQuery(id+"F15.wireOp",EDGE,"E117.MirrorCS");var subQ1=sQuery(id+"F15.wireOp",EDGE,"E116.MirrorC");var subQ2=makeQuery(id+"F15.imprint","INTERSECT",VERTEX,{"disambiguationData":[OD(0.0)],"derivedFrom":[subQ1,subQ0]});Q27=makeQuery(id+"F15.imprint","IMPRINT",FACE,{"disambiguationData":[TD([[makeQuery(id+"F15.imprint","IMPRINT",EDGE,{"disambiguationData":[TD([[subQ2,1.0]])],"derivedFrom":subQ1}),-1.0]])]});}
            var Q28;
            {var subQ0=sQuery(id+"F15.wireOp",EDGE,"E125.MirrorCS");var subQ1=sQuery(id+"F15.wireOp",EDGE,"E121.MirrorC");var subQ2=makeQuery(id+"F15.imprint","INTERSECT",VERTEX,{"disambiguationData":[OD(0.0)],"derivedFrom":[subQ1,subQ0]});Q28=makeQuery(id+"F15.imprint","IMPRINT",FACE,{"disambiguationData":[TD([[makeQuery(id+"F15.imprint","IMPRINT",EDGE,{"disambiguationData":[TD([[subQ2,1.0]])],"derivedFrom":subQ1}),-1.0]])]});}
            var Q29;
            {var subQ0=sQuery(id+"F15.wireOp",EDGE,"E130.MirrorCS");var subQ1=sQuery(id+"F15.wireOp",EDGE,"E126.MirrorC");var subQ2=makeQuery(id+"F15.imprint","INTERSECT",VERTEX,{"disambiguationData":[OD(0.0)],"derivedFrom":[subQ1,subQ0]});Q29=makeQuery(id+"F15.imprint","IMPRINT",FACE,{"disambiguationData":[TD([[makeQuery(id+"F15.imprint","IMPRINT",EDGE,{"disambiguationData":[TD([[subQ2,-1.0]])],"derivedFrom":subQ1}),-1.0]])]});}
            var Q30;
            {var subQ0=sQuery(id+"F15.wireOp",EDGE,"E135.MirrorC");var subQ1=sQuery(id+"F15.wireOp",EDGE,"E131.MirrorCS");var subQ2=makeQuery(id+"F15.imprint","INTERSECT",VERTEX,{"disambiguationData":[OD(0.0)],"derivedFrom":[subQ1,subQ0]});Q30=makeQuery(id+"F15.imprint","IMPRINT",FACE,{"disambiguationData":[TD([[makeQuery(id+"F15.imprint","IMPRINT",EDGE,{"disambiguationData":[TD([[subQ2,-1.0]])],"derivedFrom":subQ1}),-1.0]])]});}
            var Q31;
            {var subQ0=sQuery(id+"F15.wireOp",EDGE,"E139.MirrorCS");var subQ1=sQuery(id+"F15.wireOp",EDGE,"E136.MirrorC");var subQ2=makeQuery(id+"F15.imprint","INTERSECT",VERTEX,{"disambiguationData":[OD(0.0)],"derivedFrom":[subQ1,subQ0]});Q31=makeQuery(id+"F15.imprint","IMPRINT",FACE,{"disambiguationData":[TD([[makeQuery(id+"F15.imprint","IMPRINT",EDGE,{"disambiguationData":[TD([[subQ2,1.0]])],"derivedFrom":subQ1}),1.0]])]});}
            var Q32;
            {var subQ0=sQuery(id+"F15.wireOp",EDGE,"E141.1.0.4");var subQ1=sQuery(id+"F15.wireOp",EDGE,"E141.1.0.3");var subQ2=makeQuery(id+"F15.imprint","INTERSECT",VERTEX,{"disambiguationData":[OD(0.0)],"derivedFrom":[subQ1,subQ0]});Q32=makeQuery(id+"F15.imprint","IMPRINT",FACE,{"disambiguationData":[TD([[makeQuery(id+"F15.imprint","IMPRINT",EDGE,{"disambiguationData":[TD([[subQ2,-1.0]])],"derivedFrom":subQ1}),-1.0]])]});}
            var Q33;
            {var subQ0=sQuery(id+"F15.wireOp",EDGE,"E141.1.0.9");var subQ1=sQuery(id+"F15.wireOp",EDGE,"E141.1.0.8");var subQ2=makeQuery(id+"F15.imprint","INTERSECT",VERTEX,{"disambiguationData":[OD(0.0)],"derivedFrom":[subQ1,subQ0]});Q33=makeQuery(id+"F15.imprint","IMPRINT",FACE,{"disambiguationData":[TD([[makeQuery(id+"F15.imprint","IMPRINT",EDGE,{"disambiguationData":[TD([[subQ2,-1.0]])],"derivedFrom":subQ1}),-1.0]])]});}
            var Q34;
            {var subQ0=sQuery(id+"F15.wireOp",EDGE,"E141.1.0.14");var subQ1=sQuery(id+"F15.wireOp",EDGE,"E141.1.0.11");var subQ2=makeQuery(id+"F15.imprint","INTERSECT",VERTEX,{"disambiguationData":[OD(0.0)],"derivedFrom":[subQ1,subQ0]});Q34=makeQuery(id+"F15.imprint","IMPRINT",FACE,{"disambiguationData":[TD([[makeQuery(id+"F15.imprint","IMPRINT",EDGE,{"disambiguationData":[TD([[subQ2,1.0]])],"derivedFrom":subQ1}),1.0]])]});}
            var Q35;
            {var subQ0=sQuery(id+"F15.wireOp",EDGE,"E141.1.0.19");var subQ1=sQuery(id+"F15.wireOp",EDGE,"E141.1.0.17");var subQ2=makeQuery(id+"F15.imprint","INTERSECT",VERTEX,{"disambiguationData":[OD(0.0)],"derivedFrom":[subQ1,subQ0]});Q35=makeQuery(id+"F15.imprint","IMPRINT",FACE,{"disambiguationData":[TD([[makeQuery(id+"F15.imprint","IMPRINT",EDGE,{"disambiguationData":[TD([[subQ2,-1.0]])],"derivedFrom":subQ1}),1.0]])]});}
            var Q36;
            {var subQ0=sQuery(id+"F15.wireOp",EDGE,"E141.1.0.22");var subQ1=sQuery(id+"F15.wireOp",EDGE,"E141.1.0.21");var subQ2=makeQuery(id+"F15.imprint","INTERSECT",VERTEX,{"disambiguationData":[OD(0.0)],"derivedFrom":[subQ1,subQ0]});Q36=makeQuery(id+"F15.imprint","IMPRINT",FACE,{"disambiguationData":[TD([[makeQuery(id+"F15.imprint","IMPRINT",EDGE,{"disambiguationData":[TD([[subQ2,1.0]])],"derivedFrom":subQ1}),-1.0]])]});}
            var Q37;
            {var subQ0=sQuery(id+"F15.wireOp",EDGE,"E141.1.0.26");var subQ1=sQuery(id+"F15.wireOp",EDGE,"E141.1.0.25");var subQ2=makeQuery(id+"F15.imprint","INTERSECT",VERTEX,{"disambiguationData":[OD(0.0)],"derivedFrom":[subQ1,subQ0]});Q37=makeQuery(id+"F15.imprint","IMPRINT",FACE,{"disambiguationData":[TD([[makeQuery(id+"F15.imprint","IMPRINT",EDGE,{"disambiguationData":[TD([[subQ2,-1.0]])],"derivedFrom":subQ1}),-1.0]])]});}
            var Q38;
            {var subQ0=sQuery(id+"F15.wireOp",EDGE,"E141.1.0.34");var subQ1=sQuery(id+"F15.wireOp",EDGE,"E141.1.0.30");var subQ2=makeQuery(id+"F15.imprint","INTERSECT",VERTEX,{"disambiguationData":[OD(0.0)],"derivedFrom":[subQ1,subQ0]});Q38=makeQuery(id+"F15.imprint","IMPRINT",FACE,{"disambiguationData":[TD([[makeQuery(id+"F15.imprint","IMPRINT",EDGE,{"disambiguationData":[TD([[subQ2,-1.0]])],"derivedFrom":subQ1}),1.0]])]});}
            var Q39;
            {var subQ0=sQuery(id+"F15.wireOp",EDGE,"E141.1.0.39");var subQ1=sQuery(id+"F15.wireOp",EDGE,"E141.1.0.38");var subQ2=makeQuery(id+"F15.imprint","INTERSECT",VERTEX,{"disambiguationData":[OD(0.0)],"derivedFrom":[subQ1,subQ0]});Q39=makeQuery(id+"F15.imprint","IMPRINT",FACE,{"disambiguationData":[TD([[makeQuery(id+"F15.imprint","IMPRINT",EDGE,{"disambiguationData":[TD([[subQ2,1.0]])],"derivedFrom":subQ1}),1.0]])]});}
            var Q40;
            {var subQ0=sQuery(id+"F15.wireOp",EDGE,"E141.2.0.4");var subQ1=sQuery(id+"F15.wireOp",EDGE,"E141.2.0.3");var subQ2=makeQuery(id+"F15.imprint","INTERSECT",VERTEX,{"disambiguationData":[OD(0.0)],"derivedFrom":[subQ1,subQ0]});Q40=makeQuery(id+"F15.imprint","IMPRINT",FACE,{"disambiguationData":[TD([[makeQuery(id+"F15.imprint","IMPRINT",EDGE,{"disambiguationData":[TD([[subQ2,-1.0]])],"derivedFrom":subQ1}),-1.0]])]});}
            var Q41;
            {var subQ0=sQuery(id+"F15.wireOp",EDGE,"E141.2.0.9");var subQ1=sQuery(id+"F15.wireOp",EDGE,"E141.2.0.8");var subQ2=makeQuery(id+"F15.imprint","INTERSECT",VERTEX,{"disambiguationData":[OD(0.0)],"derivedFrom":[subQ1,subQ0]});Q41=makeQuery(id+"F15.imprint","IMPRINT",FACE,{"disambiguationData":[TD([[makeQuery(id+"F15.imprint","IMPRINT",EDGE,{"disambiguationData":[TD([[subQ2,-1.0]])],"derivedFrom":subQ1}),-1.0]])]});}
            var Q42;
            {var subQ0=sQuery(id+"F15.wireOp",EDGE,"E141.2.0.14");var subQ1=sQuery(id+"F15.wireOp",EDGE,"E141.2.0.11");var subQ2=makeQuery(id+"F15.imprint","INTERSECT",VERTEX,{"disambiguationData":[OD(0.0)],"derivedFrom":[subQ1,subQ0]});Q42=makeQuery(id+"F15.imprint","IMPRINT",FACE,{"disambiguationData":[TD([[makeQuery(id+"F15.imprint","IMPRINT",EDGE,{"disambiguationData":[TD([[subQ2,1.0]])],"derivedFrom":subQ1}),1.0]])]});}
            var Q43;
            {var subQ0=sQuery(id+"F15.wireOp",EDGE,"E141.2.0.19");var subQ1=sQuery(id+"F15.wireOp",EDGE,"E141.2.0.17");var subQ2=makeQuery(id+"F15.imprint","INTERSECT",VERTEX,{"disambiguationData":[OD(0.0)],"derivedFrom":[subQ1,subQ0]});Q43=makeQuery(id+"F15.imprint","IMPRINT",FACE,{"disambiguationData":[TD([[makeQuery(id+"F15.imprint","IMPRINT",EDGE,{"disambiguationData":[TD([[subQ2,-1.0]])],"derivedFrom":subQ1}),1.0]])]});}
            var Q44;
            {var subQ0=sQuery(id+"F15.wireOp",EDGE,"E141.2.0.22");var subQ1=sQuery(id+"F15.wireOp",EDGE,"E141.2.0.21");var subQ2=makeQuery(id+"F15.imprint","INTERSECT",VERTEX,{"disambiguationData":[OD(0.0)],"derivedFrom":[subQ1,subQ0]});Q44=makeQuery(id+"F15.imprint","IMPRINT",FACE,{"disambiguationData":[TD([[makeQuery(id+"F15.imprint","IMPRINT",EDGE,{"disambiguationData":[TD([[subQ2,1.0]])],"derivedFrom":subQ1}),-1.0]])]});}
            var Q45;
            {var subQ0=sQuery(id+"F15.wireOp",EDGE,"E141.2.0.26");var subQ1=sQuery(id+"F15.wireOp",EDGE,"E141.2.0.25");var subQ2=makeQuery(id+"F15.imprint","INTERSECT",VERTEX,{"disambiguationData":[OD(0.0)],"derivedFrom":[subQ1,subQ0]});Q45=makeQuery(id+"F15.imprint","IMPRINT",FACE,{"disambiguationData":[TD([[makeQuery(id+"F15.imprint","IMPRINT",EDGE,{"disambiguationData":[TD([[subQ2,-1.0]])],"derivedFrom":subQ1}),-1.0]])]});}
            var Q46;
            {var subQ0=sQuery(id+"F15.wireOp",EDGE,"E141.2.0.34");var subQ1=sQuery(id+"F15.wireOp",EDGE,"E141.2.0.30");var subQ2=makeQuery(id+"F15.imprint","INTERSECT",VERTEX,{"disambiguationData":[OD(0.0)],"derivedFrom":[subQ1,subQ0]});Q46=makeQuery(id+"F15.imprint","IMPRINT",FACE,{"disambiguationData":[TD([[makeQuery(id+"F15.imprint","IMPRINT",EDGE,{"disambiguationData":[TD([[subQ2,-1.0]])],"derivedFrom":subQ1}),1.0]])]});}
            var Q47;
            {var subQ0=sQuery(id+"F15.wireOp",EDGE,"E141.2.0.39");var subQ1=sQuery(id+"F15.wireOp",EDGE,"E141.2.0.38");var subQ2=makeQuery(id+"F15.imprint","INTERSECT",VERTEX,{"disambiguationData":[OD(0.0)],"derivedFrom":[subQ1,subQ0]});Q47=makeQuery(id+"F15.imprint","IMPRINT",FACE,{"disambiguationData":[TD([[makeQuery(id+"F15.imprint","IMPRINT",EDGE,{"disambiguationData":[TD([[subQ2,1.0]])],"derivedFrom":subQ1}),1.0]])]});}
            var Q48;
            Q48=makeQuery(id+"F14.boolean.opBoolean","MERGE",FACE,{"derivedFrom":[makeQuery(id+"F9.boolean.opBoolean","COPY",FACE,{"derivedFrom":makeQuery(id+"F9.opExtrude","CAP_FACE",FACE,{"disambiguationData":[OSD([sQuery(id+"F5.wireOp",EDGE,"E22.0"),sQuery(id+"F5.wireOp",EDGE,"E22.1"),sQuery(id+"F5.wireOp",EDGE,"E22.2"),sQuery(id+"F5.wireOp",EDGE,"E22.3"),sQuery(id+"F5.wireOp",EDGE,"E22.4"),sQuery(id+"F5.wireOp",EDGE,"E22.5"),sQuery(id+"F5.wireOp",EDGE,"E22.6"),sQuery(id+"F5.wireOp",EDGE,"E22.7")])],"isStart":true})}),makeQuery(id+"F9.boolean.opBoolean","COPY",FACE,{"derivedFrom":makeQuery(id+"F9.opExtrude","CAP_FACE",FACE,{"disambiguationData":[OSD([sQuery(id+"F5.wireOp",EDGE,"E23.0"),sQuery(id+"F5.wireOp",EDGE,"E23.1"),sQuery(id+"F5.wireOp",EDGE,"E23.2"),sQuery(id+"F5.wireOp",EDGE,"E23.3"),sQuery(id+"F5.wireOp",EDGE,"E23.4"),sQuery(id+"F5.wireOp",EDGE,"E23.5"),sQuery(id+"F5.wireOp",EDGE,"E23.6"),sQuery(id+"F5.wireOp",EDGE,"E23.7")])],"isStart":true})}),makeQuery(id+"F9.boolean.opBoolean","COPY",FACE,{"derivedFrom":makeQuery(id+"F9.opExtrude","CAP_FACE",FACE,{"disambiguationData":[OSD([sQuery(id+"F5.wireOp",EDGE,"E24.0"),sQuery(id+"F5.wireOp",EDGE,"E24.1"),sQuery(id+"F5.wireOp",EDGE,"E24.2"),sQuery(id+"F5.wireOp",EDGE,"E24.3"),sQuery(id+"F5.wireOp",EDGE,"E24.4"),sQuery(id+"F5.wireOp",EDGE,"E24.5"),sQuery(id+"F5.wireOp",EDGE,"E24.6"),sQuery(id+"F5.wireOp",EDGE,"E24.7")])],"isStart":true})}),makeQuery(id+"F14.opExtrude","SWEPT_FACE",FACE,{"disambiguationData":[OSD([sQuery(id+"F11.wireOp",EDGE,"E86")])]})]});
            extrude(context, id + "F18", {"entities" : qUnion([Q0, Q1, Q2, Q3, Q4, Q5, Q6, Q7, Q8, Q9, Q10, Q11, Q12, Q13, Q14, Q15, Q16, Q17, Q18, Q19, Q20, Q21, Q22, Q23, Q24, Q25, Q26, Q27, Q28, Q29, Q30, Q31, Q32, Q33, Q34, Q35, Q36, Q37, Q38, Q39, Q40, Q41, Q42, Q43, Q44, Q45, Q46, Q47]), "operationType" : NewBodyOperationType.REMOVE, "endBound" : BoundingType.UP_TO_SURFACE, "oppositeDirection" : true, "endBoundEntityFace" : qUnion([Q48]), "depth" : 25.4 * mm, "hasDraft" : true, "draftAngle" : 10 * degree, "draftPullDirection" : true});
        }
        {
            var Q0;
            Q0=makeQuery(id+"F7.opExtrude","SWEPT_EDGE",EDGE,{"disambiguationData":[OSD([sQuery(id+"F4.wireOp",EDGE,"E20.0"),sQuery(id+"F4.wireOp",EDGE,"E20.3")])]});
            var Q1;
            Q1=makeQuery(id+"F7.opExtrude","SWEPT_EDGE",EDGE,{"disambiguationData":[OSD([sQuery(id+"F4.wireOp",EDGE,"E20.2"),sQuery(id+"F4.wireOp",EDGE,"E20.3")])]});
            var Q2;
            Q2=makeQuery(id+"F7.opExtrude","SWEPT_EDGE",EDGE,{"disambiguationData":[OSD([sQuery(id+"F4.wireOp",EDGE,"E20.1"),sQuery(id+"F4.wireOp",EDGE,"E20.2")])]});
            var Q3;
            Q3=makeQuery(id+"F7.opExtrude","SWEPT_EDGE",EDGE,{"disambiguationData":[OSD([sQuery(id+"F4.wireOp",EDGE,"E20.0"),sQuery(id+"F4.wireOp",EDGE,"E20.1")])]});
            chamfer(context, id + "F19", {"entities" : qUnion([Q0, Q1, Q2, Q3]), "width" : 17.78 * mm, "tangentPropagation" : true});
        }
        {
            var Q0;
            Q0=makeQuery(id+"F7.opExtrude","CAP_FACE",FACE,{"disambiguationData":[OSD([sQuery(id+"F4.wireOp",EDGE,"E20.0"),sQuery(id+"F4.wireOp",EDGE,"E20.1"),sQuery(id+"F4.wireOp",EDGE,"E20.2"),sQuery(id+"F4.wireOp",EDGE,"E20.3")])],"isStart":true});
            shell(context, id + "F20", {"entities" : qUnion([Q0]), "thickness" : 1.27 * mm});
        }
    });
